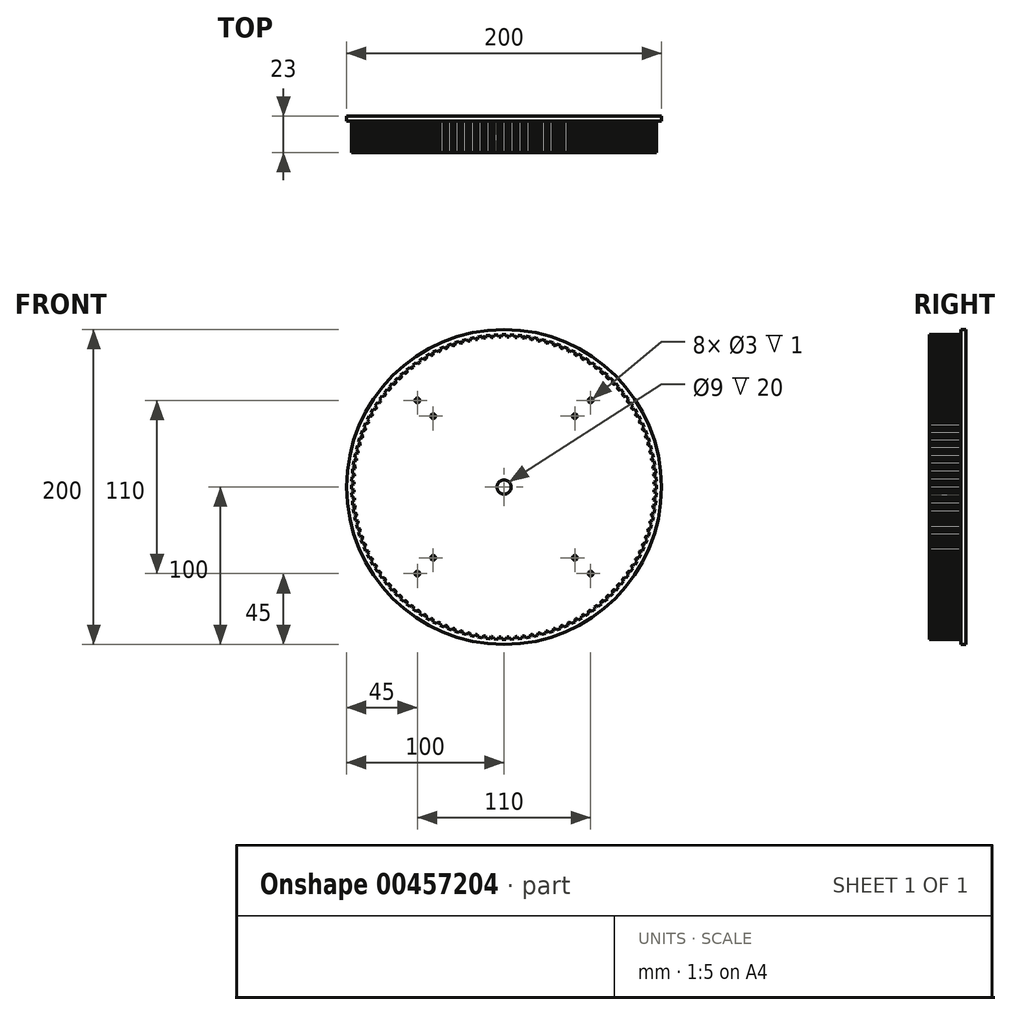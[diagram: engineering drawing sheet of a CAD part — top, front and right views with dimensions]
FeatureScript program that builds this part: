
annotation { "Feature Type Name" : "Feature", "Feature Type Description" : "" }
export const myFeature = defineFeature(function(context is Context, id is Id, definition is map)
    precondition{}
    {
        {
            var Q0;
            Q0=qCreatedBy(makeId("Front.planeOp"),FACE);
            var sketch = newSketch(context, id + "F0", { "sketchPlane" : qUnion([Q0])});
            skCircle(sketch, "E0", {"center": v(0, 0) * mm, "radius": 96.77 * mm, "construction": true});
            skLineSegment(sketch, "E1", {"start": v(0, 96.77) * mm, "end": v(0, 95.37) * mm, "construction": true});
            skCircle(sketch, "E2", {"center": v(0, 0) * mm, "radius": 95.37 * mm});
            skLineSegment(sketch, "E3", {"start": v(0, 0) * mm, "end": v(-1.27, 96.76) * mm, "construction": true});
            skLineSegment(sketch, "E4", {"start": v(0, 0) * mm, "end": v(-2.53, 96.73) * mm, "construction": true});
            skLineSegment(sketch, "E5.MirrorCS", {"start": v(0, 0) * mm, "end": v(1.27, 96.76) * mm, "construction": true});
            skLineSegment(sketch, "E6.MirrorCS", {"start": v(0, 0) * mm, "end": v(2.53, 96.73) * mm, "construction": true});
            skLineSegment(sketch, "E7", {"start": v(-1.27, 96.76) * mm, "end": v(1.27, 96.76) * mm});
            skLineSegment(sketch, "E8", {"start": v(-1.27, 96.76) * mm, "end": v(-1.88, 95.35) * mm});
            skLineSegment(sketch, "E9.MirrorCS", {"start": v(1.27, 96.76) * mm, "end": v(1.88, 95.35) * mm});
            skLineSegment(sketch, "E10.1.0", {"start": v(-6.33, 96.56) * mm, "end": v(-6.87, 95.12) * mm});
            skLineSegment(sketch, "E10.1.1", {"start": v(-6.33, 96.56) * mm, "end": v(-3.8, 96.7) * mm});
            skLineSegment(sketch, "E10.1.2", {"start": v(-3.8, 96.7) * mm, "end": v(-3.11, 95.31) * mm});
            skLineSegment(sketch, "E10.2.0", {"start": v(-11.37, 96.1) * mm, "end": v(-11.84, 94.63) * mm});
            skLineSegment(sketch, "E10.2.1", {"start": v(-11.37, 96.1) * mm, "end": v(-8.85, 96.36) * mm});
            skLineSegment(sketch, "E10.2.2", {"start": v(-8.85, 96.36) * mm, "end": v(-8.1, 95.02) * mm});
            skLineSegment(sketch, "E10.3.0", {"start": v(-16.39, 95.37) * mm, "end": v(-16.77, 93.88) * mm});
            skLineSegment(sketch, "E10.3.1", {"start": v(-16.39, 95.37) * mm, "end": v(-13.89, 95.76) * mm});
            skLineSegment(sketch, "E10.3.2", {"start": v(-13.89, 95.76) * mm, "end": v(-13.06, 94.47) * mm});
            skLineSegment(sketch, "E10.4.0", {"start": v(-21.36, 94.38) * mm, "end": v(-21.66, 92.87) * mm});
            skLineSegment(sketch, "E10.4.1", {"start": v(-21.36, 94.38) * mm, "end": v(-18.88, 94.9) * mm});
            skLineSegment(sketch, "E10.4.2", {"start": v(-18.88, 94.9) * mm, "end": v(-17.98, 93.65) * mm});
            skLineSegment(sketch, "E10.5.0", {"start": v(-26.27, 93.13) * mm, "end": v(-26.5, 91.61) * mm});
            skLineSegment(sketch, "E10.5.1", {"start": v(-26.27, 93.13) * mm, "end": v(-23.82, 93.79) * mm});
            skLineSegment(sketch, "E10.5.2", {"start": v(-23.82, 93.79) * mm, "end": v(-22.86, 92.58) * mm});
            skLineSegment(sketch, "E10.6.0", {"start": v(-31.1, 91.63) * mm, "end": v(-31.25, 90.1) * mm});
            skLineSegment(sketch, "E10.6.1", {"start": v(-31.1, 91.63) * mm, "end": v(-28.7, 92.41) * mm});
            skLineSegment(sketch, "E10.6.2", {"start": v(-28.7, 92.41) * mm, "end": v(-27.68, 91.26) * mm});
            skLineSegment(sketch, "E10.7.0", {"start": v(-35.86, 89.88) * mm, "end": v(-35.92, 88.34) * mm});
            skLineSegment(sketch, "E10.7.1", {"start": v(-35.86, 89.88) * mm, "end": v(-33.5, 90.78) * mm});
            skLineSegment(sketch, "E10.7.2", {"start": v(-33.5, 90.78) * mm, "end": v(-32.41, 89.69) * mm});
            skLineSegment(sketch, "E10.8.0", {"start": v(-40.51, 87.88) * mm, "end": v(-40.5, 86.34) * mm});
            skLineSegment(sketch, "E10.8.1", {"start": v(-40.51, 87.88) * mm, "end": v(-38.2, 88.9) * mm});
            skLineSegment(sketch, "E10.8.2", {"start": v(-38.2, 88.9) * mm, "end": v(-37.06, 87.87) * mm});
            skLineSegment(sketch, "E10.9.0", {"start": v(-45.06, 85.64) * mm, "end": v(-44.96, 84.1) * mm});
            skLineSegment(sketch, "E10.9.1", {"start": v(-45.06, 85.64) * mm, "end": v(-42.8, 86.79) * mm});
            skLineSegment(sketch, "E10.9.2", {"start": v(-42.8, 86.79) * mm, "end": v(-41.61, 85.8) * mm});
            skLineSegment(sketch, "E11", {"start": v(0, 0) * mm, "end": v(0, 96.77) * mm, "construction": true});
            skLineSegment(sketch, "E12.2.10.0", {"start": v(-49.48, 83.16) * mm, "end": v(-49.3, 81.63) * mm});
            skLineSegment(sketch, "E12.3.10.0", {"start": v(-49.48, 83.16) * mm, "end": v(-47.28, 84.43) * mm});
            skLineSegment(sketch, "E12.6.10.0", {"start": v(-47.28, 84.43) * mm, "end": v(-46.05, 83.51) * mm});
            skLineSegment(sketch, "E12.2.11.0", {"start": v(-53.76, 80.46) * mm, "end": v(-53.5, 78.94) * mm});
            skLineSegment(sketch, "E12.3.11.0", {"start": v(-53.76, 80.46) * mm, "end": v(-51.64, 81.84) * mm});
            skLineSegment(sketch, "E12.6.11.0", {"start": v(-51.64, 81.84) * mm, "end": v(-50.35, 80.99) * mm});
            skLineSegment(sketch, "E12.2.12.0", {"start": v(-57.9, 77.53) * mm, "end": v(-57.56, 76.03) * mm});
            skLineSegment(sketch, "E12.3.12.0", {"start": v(-57.9, 77.53) * mm, "end": v(-55.85, 79.02) * mm});
            skLineSegment(sketch, "E12.6.12.0", {"start": v(-55.85, 79.02) * mm, "end": v(-54.52, 78.24) * mm});
            skLineSegment(sketch, "E12.2.13.0", {"start": v(-61.88, 74.4) * mm, "end": v(-61.46, 72.92) * mm});
            skLineSegment(sketch, "E12.3.13.0", {"start": v(-61.88, 74.4) * mm, "end": v(-59.9, 76) * mm});
            skLineSegment(sketch, "E12.6.13.0", {"start": v(-59.9, 76) * mm, "end": v(-58.54, 75.28) * mm});
            skLineSegment(sketch, "E12.2.14.0", {"start": v(-65.68, 71.06) * mm, "end": v(-65.2, 69.6) * mm});
            skLineSegment(sketch, "E12.3.14.0", {"start": v(-65.68, 71.06) * mm, "end": v(-63.8, 72.75) * mm});
            skLineSegment(sketch, "E12.6.14.0", {"start": v(-63.8, 72.75) * mm, "end": v(-62.4, 72.11) * mm});
            skLineSegment(sketch, "E12.2.15.0", {"start": v(-69.31, 67.52) * mm, "end": v(-68.75, 66.1) * mm});
            skLineSegment(sketch, "E12.3.15.0", {"start": v(-69.31, 67.52) * mm, "end": v(-67.52, 69.31) * mm});
            skLineSegment(sketch, "E12.6.15.0", {"start": v(-67.52, 69.31) * mm, "end": v(-66.1, 68.75) * mm});
            skLineSegment(sketch, "E12.2.16.0", {"start": v(-72.75, 63.8) * mm, "end": v(-72.11, 62.4) * mm});
            skLineSegment(sketch, "E12.3.16.0", {"start": v(-72.75, 63.8) * mm, "end": v(-71.06, 65.68) * mm});
            skLineSegment(sketch, "E12.6.16.0", {"start": v(-71.06, 65.68) * mm, "end": v(-69.6, 65.2) * mm});
            skLineSegment(sketch, "E12.2.17.0", {"start": v(-76, 59.9) * mm, "end": v(-75.28, 58.54) * mm});
            skLineSegment(sketch, "E12.3.17.0", {"start": v(-76, 59.9) * mm, "end": v(-74.4, 61.88) * mm});
            skLineSegment(sketch, "E12.6.17.0", {"start": v(-74.4, 61.88) * mm, "end": v(-72.92, 61.46) * mm});
            skLineSegment(sketch, "E12.2.18.0", {"start": v(-79.02, 55.85) * mm, "end": v(-78.24, 54.52) * mm});
            skLineSegment(sketch, "E12.3.18.0", {"start": v(-79.02, 55.85) * mm, "end": v(-77.53, 57.9) * mm});
            skLineSegment(sketch, "E12.6.18.0", {"start": v(-77.53, 57.9) * mm, "end": v(-76.03, 57.56) * mm});
            skLineSegment(sketch, "E12.2.19.0", {"start": v(-81.84, 51.64) * mm, "end": v(-80.99, 50.35) * mm});
            skLineSegment(sketch, "E12.3.19.0", {"start": v(-81.84, 51.64) * mm, "end": v(-80.46, 53.76) * mm});
            skLineSegment(sketch, "E12.6.19.0", {"start": v(-80.46, 53.76) * mm, "end": v(-78.94, 53.5) * mm});
            skLineSegment(sketch, "E12.2.20.0", {"start": v(-84.43, 47.28) * mm, "end": v(-83.51, 46.05) * mm});
            skLineSegment(sketch, "E12.3.20.0", {"start": v(-84.43, 47.28) * mm, "end": v(-83.16, 49.48) * mm});
            skLineSegment(sketch, "E12.6.20.0", {"start": v(-83.16, 49.48) * mm, "end": v(-81.63, 49.3) * mm});
            skLineSegment(sketch, "E12.2.21.0", {"start": v(-86.79, 42.8) * mm, "end": v(-85.8, 41.61) * mm});
            skLineSegment(sketch, "E12.3.21.0", {"start": v(-86.79, 42.8) * mm, "end": v(-85.64, 45.06) * mm});
            skLineSegment(sketch, "E12.6.21.0", {"start": v(-85.64, 45.06) * mm, "end": v(-84.1, 44.96) * mm});
            skLineSegment(sketch, "E12.2.22.0", {"start": v(-88.9, 38.2) * mm, "end": v(-87.87, 37.06) * mm});
            skLineSegment(sketch, "E12.3.22.0", {"start": v(-88.9, 38.2) * mm, "end": v(-87.88, 40.51) * mm});
            skLineSegment(sketch, "E12.6.22.0", {"start": v(-87.88, 40.51) * mm, "end": v(-86.34, 40.5) * mm});
            skLineSegment(sketch, "E12.2.23.0", {"start": v(-90.78, 33.5) * mm, "end": v(-89.69, 32.41) * mm});
            skLineSegment(sketch, "E12.3.23.0", {"start": v(-90.78, 33.5) * mm, "end": v(-89.88, 35.86) * mm});
            skLineSegment(sketch, "E12.6.23.0", {"start": v(-89.88, 35.86) * mm, "end": v(-88.34, 35.92) * mm});
            skLineSegment(sketch, "E12.2.24.0", {"start": v(-92.41, 28.7) * mm, "end": v(-91.26, 27.68) * mm});
            skLineSegment(sketch, "E12.3.24.0", {"start": v(-92.41, 28.7) * mm, "end": v(-91.63, 31.1) * mm});
            skLineSegment(sketch, "E12.6.24.0", {"start": v(-91.63, 31.1) * mm, "end": v(-90.1, 31.25) * mm});
            skLineSegment(sketch, "E12.2.25.0", {"start": v(-93.79, 23.82) * mm, "end": v(-92.58, 22.86) * mm});
            skLineSegment(sketch, "E12.3.25.0", {"start": v(-93.79, 23.82) * mm, "end": v(-93.13, 26.27) * mm});
            skLineSegment(sketch, "E12.6.25.0", {"start": v(-93.13, 26.27) * mm, "end": v(-91.61, 26.5) * mm});
            skLineSegment(sketch, "E12.2.26.0", {"start": v(-94.9, 18.88) * mm, "end": v(-93.65, 17.98) * mm});
            skLineSegment(sketch, "E12.3.26.0", {"start": v(-94.9, 18.88) * mm, "end": v(-94.38, 21.36) * mm});
            skLineSegment(sketch, "E12.6.26.0", {"start": v(-94.38, 21.36) * mm, "end": v(-92.87, 21.66) * mm});
            skLineSegment(sketch, "E12.2.27.0", {"start": v(-95.76, 13.89) * mm, "end": v(-94.47, 13.06) * mm});
            skLineSegment(sketch, "E12.3.27.0", {"start": v(-95.76, 13.89) * mm, "end": v(-95.37, 16.39) * mm});
            skLineSegment(sketch, "E12.6.27.0", {"start": v(-95.37, 16.39) * mm, "end": v(-93.88, 16.77) * mm});
            skLineSegment(sketch, "E12.2.28.0", {"start": v(-96.36, 8.85) * mm, "end": v(-95.02, 8.1) * mm});
            skLineSegment(sketch, "E12.3.28.0", {"start": v(-96.36, 8.85) * mm, "end": v(-96.1, 11.37) * mm});
            skLineSegment(sketch, "E12.6.28.0", {"start": v(-96.1, 11.37) * mm, "end": v(-94.63, 11.84) * mm});
            skLineSegment(sketch, "E12.2.29.0", {"start": v(-96.7, 3.8) * mm, "end": v(-95.31, 3.11) * mm});
            skLineSegment(sketch, "E12.3.29.0", {"start": v(-96.7, 3.8) * mm, "end": v(-96.56, 6.33) * mm});
            skLineSegment(sketch, "E12.6.29.0", {"start": v(-96.56, 6.33) * mm, "end": v(-95.12, 6.87) * mm});
            skLineSegment(sketch, "E12.2.30.0", {"start": v(-96.76, -1.27) * mm, "end": v(-95.35, -1.88) * mm});
            skLineSegment(sketch, "E12.3.30.0", {"start": v(-96.76, -1.27) * mm, "end": v(-96.76, 1.27) * mm});
            skLineSegment(sketch, "E12.6.30.0", {"start": v(-96.76, 1.27) * mm, "end": v(-95.35, 1.88) * mm});
            skLineSegment(sketch, "E12.2.31.0", {"start": v(-96.56, -6.33) * mm, "end": v(-95.12, -6.87) * mm});
            skLineSegment(sketch, "E12.3.31.0", {"start": v(-96.56, -6.33) * mm, "end": v(-96.7, -3.8) * mm});
            skLineSegment(sketch, "E12.6.31.0", {"start": v(-96.7, -3.8) * mm, "end": v(-95.31, -3.11) * mm});
            skLineSegment(sketch, "E12.2.32.0", {"start": v(-96.1, -11.37) * mm, "end": v(-94.63, -11.84) * mm});
            skLineSegment(sketch, "E12.3.32.0", {"start": v(-96.1, -11.37) * mm, "end": v(-96.36, -8.85) * mm});
            skLineSegment(sketch, "E12.6.32.0", {"start": v(-96.36, -8.85) * mm, "end": v(-95.02, -8.1) * mm});
            skLineSegment(sketch, "E12.2.33.0", {"start": v(-95.37, -16.39) * mm, "end": v(-93.88, -16.77) * mm});
            skLineSegment(sketch, "E12.3.33.0", {"start": v(-95.37, -16.39) * mm, "end": v(-95.76, -13.89) * mm});
            skLineSegment(sketch, "E12.6.33.0", {"start": v(-95.76, -13.89) * mm, "end": v(-94.47, -13.06) * mm});
            skLineSegment(sketch, "E12.2.34.0", {"start": v(-94.38, -21.36) * mm, "end": v(-92.87, -21.66) * mm});
            skLineSegment(sketch, "E12.3.34.0", {"start": v(-94.38, -21.36) * mm, "end": v(-94.9, -18.88) * mm});
            skLineSegment(sketch, "E12.6.34.0", {"start": v(-94.9, -18.88) * mm, "end": v(-93.65, -17.98) * mm});
            skLineSegment(sketch, "E12.2.35.0", {"start": v(-93.13, -26.27) * mm, "end": v(-91.61, -26.5) * mm});
            skLineSegment(sketch, "E12.3.35.0", {"start": v(-93.13, -26.27) * mm, "end": v(-93.79, -23.82) * mm});
            skLineSegment(sketch, "E12.6.35.0", {"start": v(-93.79, -23.82) * mm, "end": v(-92.58, -22.86) * mm});
            skLineSegment(sketch, "E12.2.36.0", {"start": v(-91.63, -31.1) * mm, "end": v(-90.1, -31.25) * mm});
            skLineSegment(sketch, "E12.3.36.0", {"start": v(-91.63, -31.1) * mm, "end": v(-92.41, -28.7) * mm});
            skLineSegment(sketch, "E12.6.36.0", {"start": v(-92.41, -28.7) * mm, "end": v(-91.26, -27.68) * mm});
            skLineSegment(sketch, "E12.2.37.0", {"start": v(-89.88, -35.86) * mm, "end": v(-88.34, -35.92) * mm});
            skLineSegment(sketch, "E12.3.37.0", {"start": v(-89.88, -35.86) * mm, "end": v(-90.78, -33.5) * mm});
            skLineSegment(sketch, "E12.6.37.0", {"start": v(-90.78, -33.5) * mm, "end": v(-89.69, -32.41) * mm});
            skLineSegment(sketch, "E12.2.38.0", {"start": v(-87.88, -40.51) * mm, "end": v(-86.34, -40.5) * mm});
            skLineSegment(sketch, "E12.3.38.0", {"start": v(-87.88, -40.51) * mm, "end": v(-88.9, -38.2) * mm});
            skLineSegment(sketch, "E12.6.38.0", {"start": v(-88.9, -38.2) * mm, "end": v(-87.87, -37.06) * mm});
            skLineSegment(sketch, "E12.2.39.0", {"start": v(-85.64, -45.06) * mm, "end": v(-84.1, -44.96) * mm});
            skLineSegment(sketch, "E12.3.39.0", {"start": v(-85.64, -45.06) * mm, "end": v(-86.79, -42.8) * mm});
            skLineSegment(sketch, "E12.6.39.0", {"start": v(-86.79, -42.8) * mm, "end": v(-85.8, -41.61) * mm});
            skLineSegment(sketch, "E12.2.40.0", {"start": v(-83.16, -49.48) * mm, "end": v(-81.63, -49.3) * mm});
            skLineSegment(sketch, "E12.3.40.0", {"start": v(-83.16, -49.48) * mm, "end": v(-84.43, -47.28) * mm});
            skLineSegment(sketch, "E12.6.40.0", {"start": v(-84.43, -47.28) * mm, "end": v(-83.51, -46.05) * mm});
            skLineSegment(sketch, "E12.2.41.0", {"start": v(-80.46, -53.76) * mm, "end": v(-78.94, -53.5) * mm});
            skLineSegment(sketch, "E12.3.41.0", {"start": v(-80.46, -53.76) * mm, "end": v(-81.84, -51.64) * mm});
            skLineSegment(sketch, "E12.6.41.0", {"start": v(-81.84, -51.64) * mm, "end": v(-80.99, -50.35) * mm});
            skLineSegment(sketch, "E12.2.42.0", {"start": v(-77.53, -57.9) * mm, "end": v(-76.03, -57.56) * mm});
            skLineSegment(sketch, "E12.3.42.0", {"start": v(-77.53, -57.9) * mm, "end": v(-79.02, -55.85) * mm});
            skLineSegment(sketch, "E12.6.42.0", {"start": v(-79.02, -55.85) * mm, "end": v(-78.24, -54.52) * mm});
            skLineSegment(sketch, "E12.2.43.0", {"start": v(-74.4, -61.88) * mm, "end": v(-72.92, -61.46) * mm});
            skLineSegment(sketch, "E12.3.43.0", {"start": v(-74.4, -61.88) * mm, "end": v(-76, -59.9) * mm});
            skLineSegment(sketch, "E12.6.43.0", {"start": v(-76, -59.9) * mm, "end": v(-75.28, -58.54) * mm});
            skLineSegment(sketch, "E12.2.44.0", {"start": v(-71.06, -65.68) * mm, "end": v(-69.6, -65.2) * mm});
            skLineSegment(sketch, "E12.3.44.0", {"start": v(-71.06, -65.68) * mm, "end": v(-72.75, -63.8) * mm});
            skLineSegment(sketch, "E12.6.44.0", {"start": v(-72.75, -63.8) * mm, "end": v(-72.11, -62.4) * mm});
            skLineSegment(sketch, "E12.2.45.0", {"start": v(-67.52, -69.31) * mm, "end": v(-66.1, -68.75) * mm});
            skLineSegment(sketch, "E12.3.45.0", {"start": v(-67.52, -69.31) * mm, "end": v(-69.31, -67.52) * mm});
            skLineSegment(sketch, "E12.6.45.0", {"start": v(-69.31, -67.52) * mm, "end": v(-68.75, -66.1) * mm});
            skLineSegment(sketch, "E12.2.46.0", {"start": v(-63.8, -72.75) * mm, "end": v(-62.4, -72.11) * mm});
            skLineSegment(sketch, "E12.3.46.0", {"start": v(-63.8, -72.75) * mm, "end": v(-65.68, -71.06) * mm});
            skLineSegment(sketch, "E12.6.46.0", {"start": v(-65.68, -71.06) * mm, "end": v(-65.2, -69.6) * mm});
            skLineSegment(sketch, "E12.2.47.0", {"start": v(-59.9, -76) * mm, "end": v(-58.54, -75.28) * mm});
            skLineSegment(sketch, "E12.3.47.0", {"start": v(-59.9, -76) * mm, "end": v(-61.88, -74.4) * mm});
            skLineSegment(sketch, "E12.6.47.0", {"start": v(-61.88, -74.4) * mm, "end": v(-61.46, -72.92) * mm});
            skLineSegment(sketch, "E12.2.48.0", {"start": v(-55.85, -79.02) * mm, "end": v(-54.52, -78.24) * mm});
            skLineSegment(sketch, "E12.3.48.0", {"start": v(-55.85, -79.02) * mm, "end": v(-57.9, -77.53) * mm});
            skLineSegment(sketch, "E12.6.48.0", {"start": v(-57.9, -77.53) * mm, "end": v(-57.56, -76.03) * mm});
            skLineSegment(sketch, "E12.2.49.0", {"start": v(-51.64, -81.84) * mm, "end": v(-50.35, -80.99) * mm});
            skLineSegment(sketch, "E12.3.49.0", {"start": v(-51.64, -81.84) * mm, "end": v(-53.76, -80.46) * mm});
            skLineSegment(sketch, "E12.6.49.0", {"start": v(-53.76, -80.46) * mm, "end": v(-53.5, -78.94) * mm});
            skLineSegment(sketch, "E12.2.50.0", {"start": v(-47.28, -84.43) * mm, "end": v(-46.05, -83.51) * mm});
            skLineSegment(sketch, "E12.3.50.0", {"start": v(-47.28, -84.43) * mm, "end": v(-49.48, -83.16) * mm});
            skLineSegment(sketch, "E12.6.50.0", {"start": v(-49.48, -83.16) * mm, "end": v(-49.3, -81.63) * mm});
            skLineSegment(sketch, "E12.2.51.0", {"start": v(-42.8, -86.79) * mm, "end": v(-41.61, -85.8) * mm});
            skLineSegment(sketch, "E12.3.51.0", {"start": v(-42.8, -86.79) * mm, "end": v(-45.06, -85.64) * mm});
            skLineSegment(sketch, "E12.6.51.0", {"start": v(-45.06, -85.64) * mm, "end": v(-44.96, -84.1) * mm});
            skLineSegment(sketch, "E12.2.52.0", {"start": v(-38.2, -88.9) * mm, "end": v(-37.06, -87.87) * mm});
            skLineSegment(sketch, "E12.3.52.0", {"start": v(-38.2, -88.9) * mm, "end": v(-40.51, -87.88) * mm});
            skLineSegment(sketch, "E12.6.52.0", {"start": v(-40.51, -87.88) * mm, "end": v(-40.5, -86.34) * mm});
            skLineSegment(sketch, "E12.2.53.0", {"start": v(-33.5, -90.78) * mm, "end": v(-32.41, -89.69) * mm});
            skLineSegment(sketch, "E12.3.53.0", {"start": v(-33.5, -90.78) * mm, "end": v(-35.86, -89.88) * mm});
            skLineSegment(sketch, "E12.6.53.0", {"start": v(-35.86, -89.88) * mm, "end": v(-35.92, -88.34) * mm});
            skLineSegment(sketch, "E12.2.54.0", {"start": v(-28.7, -92.41) * mm, "end": v(-27.68, -91.26) * mm});
            skLineSegment(sketch, "E12.3.54.0", {"start": v(-28.7, -92.41) * mm, "end": v(-31.1, -91.63) * mm});
            skLineSegment(sketch, "E12.6.54.0", {"start": v(-31.1, -91.63) * mm, "end": v(-31.25, -90.1) * mm});
            skLineSegment(sketch, "E12.2.55.0", {"start": v(-23.82, -93.79) * mm, "end": v(-22.86, -92.58) * mm});
            skLineSegment(sketch, "E12.3.55.0", {"start": v(-23.82, -93.79) * mm, "end": v(-26.27, -93.13) * mm});
            skLineSegment(sketch, "E12.6.55.0", {"start": v(-26.27, -93.13) * mm, "end": v(-26.5, -91.61) * mm});
            skLineSegment(sketch, "E12.2.56.0", {"start": v(-18.88, -94.9) * mm, "end": v(-17.98, -93.65) * mm});
            skLineSegment(sketch, "E12.3.56.0", {"start": v(-18.88, -94.9) * mm, "end": v(-21.36, -94.38) * mm});
            skLineSegment(sketch, "E12.6.56.0", {"start": v(-21.36, -94.38) * mm, "end": v(-21.66, -92.87) * mm});
            skLineSegment(sketch, "E12.2.57.0", {"start": v(-13.89, -95.76) * mm, "end": v(-13.06, -94.47) * mm});
            skLineSegment(sketch, "E12.3.57.0", {"start": v(-13.89, -95.76) * mm, "end": v(-16.39, -95.37) * mm});
            skLineSegment(sketch, "E12.6.57.0", {"start": v(-16.39, -95.37) * mm, "end": v(-16.77, -93.88) * mm});
            skLineSegment(sketch, "E12.2.58.0", {"start": v(-8.85, -96.36) * mm, "end": v(-8.1, -95.02) * mm});
            skLineSegment(sketch, "E12.3.58.0", {"start": v(-8.85, -96.36) * mm, "end": v(-11.37, -96.1) * mm});
            skLineSegment(sketch, "E12.6.58.0", {"start": v(-11.37, -96.1) * mm, "end": v(-11.84, -94.63) * mm});
            skLineSegment(sketch, "E12.2.59.0", {"start": v(-3.8, -96.7) * mm, "end": v(-3.11, -95.31) * mm});
            skLineSegment(sketch, "E12.3.59.0", {"start": v(-3.8, -96.7) * mm, "end": v(-6.33, -96.56) * mm});
            skLineSegment(sketch, "E12.6.59.0", {"start": v(-6.33, -96.56) * mm, "end": v(-6.87, -95.12) * mm});
            skLineSegment(sketch, "E13.2.60.0", {"start": v(1.27, -96.76) * mm, "end": v(1.88, -95.35) * mm});
            skLineSegment(sketch, "E13.3.60.0", {"start": v(1.27, -96.76) * mm, "end": v(-1.27, -96.76) * mm});
            skLineSegment(sketch, "E13.6.60.0", {"start": v(-1.27, -96.76) * mm, "end": v(-1.88, -95.35) * mm});
            skLineSegment(sketch, "E13.2.61.0", {"start": v(6.33, -96.56) * mm, "end": v(6.87, -95.12) * mm});
            skLineSegment(sketch, "E13.3.61.0", {"start": v(6.33, -96.56) * mm, "end": v(3.8, -96.7) * mm});
            skLineSegment(sketch, "E13.6.61.0", {"start": v(3.8, -96.7) * mm, "end": v(3.11, -95.31) * mm});
            skLineSegment(sketch, "E13.2.62.0", {"start": v(11.37, -96.1) * mm, "end": v(11.84, -94.63) * mm});
            skLineSegment(sketch, "E13.3.62.0", {"start": v(11.37, -96.1) * mm, "end": v(8.85, -96.36) * mm});
            skLineSegment(sketch, "E13.6.62.0", {"start": v(8.85, -96.36) * mm, "end": v(8.1, -95.02) * mm});
            skLineSegment(sketch, "E13.2.63.0", {"start": v(16.39, -95.37) * mm, "end": v(16.77, -93.88) * mm});
            skLineSegment(sketch, "E13.3.63.0", {"start": v(16.39, -95.37) * mm, "end": v(13.89, -95.76) * mm});
            skLineSegment(sketch, "E13.6.63.0", {"start": v(13.89, -95.76) * mm, "end": v(13.06, -94.47) * mm});
            skLineSegment(sketch, "E13.2.64.0", {"start": v(21.36, -94.38) * mm, "end": v(21.66, -92.87) * mm});
            skLineSegment(sketch, "E13.3.64.0", {"start": v(21.36, -94.38) * mm, "end": v(18.88, -94.9) * mm});
            skLineSegment(sketch, "E13.6.64.0", {"start": v(18.88, -94.9) * mm, "end": v(17.98, -93.65) * mm});
            skLineSegment(sketch, "E13.2.65.0", {"start": v(26.27, -93.13) * mm, "end": v(26.5, -91.61) * mm});
            skLineSegment(sketch, "E13.3.65.0", {"start": v(26.27, -93.13) * mm, "end": v(23.82, -93.79) * mm});
            skLineSegment(sketch, "E13.6.65.0", {"start": v(23.82, -93.79) * mm, "end": v(22.86, -92.58) * mm});
            skLineSegment(sketch, "E13.2.66.0", {"start": v(31.1, -91.63) * mm, "end": v(31.25, -90.1) * mm});
            skLineSegment(sketch, "E13.3.66.0", {"start": v(31.1, -91.63) * mm, "end": v(28.7, -92.41) * mm});
            skLineSegment(sketch, "E13.6.66.0", {"start": v(28.7, -92.41) * mm, "end": v(27.68, -91.26) * mm});
            skLineSegment(sketch, "E13.2.67.0", {"start": v(35.86, -89.88) * mm, "end": v(35.92, -88.34) * mm});
            skLineSegment(sketch, "E13.3.67.0", {"start": v(35.86, -89.88) * mm, "end": v(33.5, -90.78) * mm});
            skLineSegment(sketch, "E13.6.67.0", {"start": v(33.5, -90.78) * mm, "end": v(32.41, -89.69) * mm});
            skLineSegment(sketch, "E13.2.68.0", {"start": v(40.51, -87.88) * mm, "end": v(40.5, -86.34) * mm});
            skLineSegment(sketch, "E13.3.68.0", {"start": v(40.51, -87.88) * mm, "end": v(38.2, -88.9) * mm});
            skLineSegment(sketch, "E13.6.68.0", {"start": v(38.2, -88.9) * mm, "end": v(37.06, -87.87) * mm});
            skLineSegment(sketch, "E13.2.69.0", {"start": v(45.06, -85.64) * mm, "end": v(44.96, -84.1) * mm});
            skLineSegment(sketch, "E13.3.69.0", {"start": v(45.06, -85.64) * mm, "end": v(42.8, -86.79) * mm});
            skLineSegment(sketch, "E13.6.69.0", {"start": v(42.8, -86.79) * mm, "end": v(41.61, -85.8) * mm});
            skLineSegment(sketch, "E13.2.70.0", {"start": v(49.48, -83.16) * mm, "end": v(49.3, -81.63) * mm});
            skLineSegment(sketch, "E13.3.70.0", {"start": v(49.48, -83.16) * mm, "end": v(47.28, -84.43) * mm});
            skLineSegment(sketch, "E13.6.70.0", {"start": v(47.28, -84.43) * mm, "end": v(46.05, -83.51) * mm});
            skLineSegment(sketch, "E13.2.71.0", {"start": v(53.76, -80.46) * mm, "end": v(53.5, -78.94) * mm});
            skLineSegment(sketch, "E13.3.71.0", {"start": v(53.76, -80.46) * mm, "end": v(51.64, -81.84) * mm});
            skLineSegment(sketch, "E13.6.71.0", {"start": v(51.64, -81.84) * mm, "end": v(50.35, -80.99) * mm});
            skLineSegment(sketch, "E13.2.72.0", {"start": v(57.9, -77.53) * mm, "end": v(57.56, -76.03) * mm});
            skLineSegment(sketch, "E13.3.72.0", {"start": v(57.9, -77.53) * mm, "end": v(55.85, -79.02) * mm});
            skLineSegment(sketch, "E13.6.72.0", {"start": v(55.85, -79.02) * mm, "end": v(54.52, -78.24) * mm});
            skLineSegment(sketch, "E13.2.73.0", {"start": v(61.88, -74.4) * mm, "end": v(61.46, -72.92) * mm});
            skLineSegment(sketch, "E13.3.73.0", {"start": v(61.88, -74.4) * mm, "end": v(59.9, -76) * mm});
            skLineSegment(sketch, "E13.6.73.0", {"start": v(59.9, -76) * mm, "end": v(58.54, -75.28) * mm});
            skLineSegment(sketch, "E13.2.74.0", {"start": v(65.68, -71.06) * mm, "end": v(65.2, -69.6) * mm});
            skLineSegment(sketch, "E13.3.74.0", {"start": v(65.68, -71.06) * mm, "end": v(63.8, -72.75) * mm});
            skLineSegment(sketch, "E13.6.74.0", {"start": v(63.8, -72.75) * mm, "end": v(62.4, -72.11) * mm});
            skLineSegment(sketch, "E13.2.75.0", {"start": v(69.31, -67.52) * mm, "end": v(68.75, -66.1) * mm});
            skLineSegment(sketch, "E13.3.75.0", {"start": v(69.31, -67.52) * mm, "end": v(67.52, -69.31) * mm});
            skLineSegment(sketch, "E13.6.75.0", {"start": v(67.52, -69.31) * mm, "end": v(66.1, -68.75) * mm});
            skLineSegment(sketch, "E13.2.76.0", {"start": v(72.75, -63.8) * mm, "end": v(72.11, -62.4) * mm});
            skLineSegment(sketch, "E13.3.76.0", {"start": v(72.75, -63.8) * mm, "end": v(71.06, -65.68) * mm});
            skLineSegment(sketch, "E13.6.76.0", {"start": v(71.06, -65.68) * mm, "end": v(69.6, -65.2) * mm});
            skLineSegment(sketch, "E13.2.77.0", {"start": v(76, -59.9) * mm, "end": v(75.28, -58.54) * mm});
            skLineSegment(sketch, "E13.3.77.0", {"start": v(76, -59.9) * mm, "end": v(74.4, -61.88) * mm});
            skLineSegment(sketch, "E13.6.77.0", {"start": v(74.4, -61.88) * mm, "end": v(72.92, -61.46) * mm});
            skLineSegment(sketch, "E13.2.78.0", {"start": v(79.02, -55.85) * mm, "end": v(78.24, -54.52) * mm});
            skLineSegment(sketch, "E13.3.78.0", {"start": v(79.02, -55.85) * mm, "end": v(77.53, -57.9) * mm});
            skLineSegment(sketch, "E13.6.78.0", {"start": v(77.53, -57.9) * mm, "end": v(76.03, -57.56) * mm});
            skLineSegment(sketch, "E13.2.79.0", {"start": v(81.84, -51.64) * mm, "end": v(80.99, -50.35) * mm});
            skLineSegment(sketch, "E13.3.79.0", {"start": v(81.84, -51.64) * mm, "end": v(80.46, -53.76) * mm});
            skLineSegment(sketch, "E13.6.79.0", {"start": v(80.46, -53.76) * mm, "end": v(78.94, -53.5) * mm});
            skLineSegment(sketch, "E13.2.80.0", {"start": v(84.43, -47.28) * mm, "end": v(83.51, -46.05) * mm});
            skLineSegment(sketch, "E13.3.80.0", {"start": v(84.43, -47.28) * mm, "end": v(83.16, -49.48) * mm});
            skLineSegment(sketch, "E13.6.80.0", {"start": v(83.16, -49.48) * mm, "end": v(81.63, -49.3) * mm});
            skLineSegment(sketch, "E13.2.81.0", {"start": v(86.79, -42.8) * mm, "end": v(85.8, -41.61) * mm});
            skLineSegment(sketch, "E13.3.81.0", {"start": v(86.79, -42.8) * mm, "end": v(85.64, -45.06) * mm});
            skLineSegment(sketch, "E13.6.81.0", {"start": v(85.64, -45.06) * mm, "end": v(84.1, -44.96) * mm});
            skLineSegment(sketch, "E13.2.82.0", {"start": v(88.9, -38.2) * mm, "end": v(87.87, -37.06) * mm});
            skLineSegment(sketch, "E13.3.82.0", {"start": v(88.9, -38.2) * mm, "end": v(87.88, -40.51) * mm});
            skLineSegment(sketch, "E13.6.82.0", {"start": v(87.88, -40.51) * mm, "end": v(86.34, -40.5) * mm});
            skLineSegment(sketch, "E13.2.83.0", {"start": v(90.78, -33.5) * mm, "end": v(89.69, -32.41) * mm});
            skLineSegment(sketch, "E13.3.83.0", {"start": v(90.78, -33.5) * mm, "end": v(89.88, -35.86) * mm});
            skLineSegment(sketch, "E13.6.83.0", {"start": v(89.88, -35.86) * mm, "end": v(88.34, -35.92) * mm});
            skLineSegment(sketch, "E13.2.84.0", {"start": v(92.41, -28.7) * mm, "end": v(91.26, -27.68) * mm});
            skLineSegment(sketch, "E13.3.84.0", {"start": v(92.41, -28.7) * mm, "end": v(91.63, -31.1) * mm});
            skLineSegment(sketch, "E13.6.84.0", {"start": v(91.63, -31.1) * mm, "end": v(90.1, -31.25) * mm});
            skLineSegment(sketch, "E13.2.85.0", {"start": v(93.79, -23.82) * mm, "end": v(92.58, -22.86) * mm});
            skLineSegment(sketch, "E13.3.85.0", {"start": v(93.79, -23.82) * mm, "end": v(93.13, -26.27) * mm});
            skLineSegment(sketch, "E13.6.85.0", {"start": v(93.13, -26.27) * mm, "end": v(91.61, -26.5) * mm});
            skLineSegment(sketch, "E13.2.86.0", {"start": v(94.9, -18.88) * mm, "end": v(93.65, -17.98) * mm});
            skLineSegment(sketch, "E13.3.86.0", {"start": v(94.9, -18.88) * mm, "end": v(94.38, -21.36) * mm});
            skLineSegment(sketch, "E13.6.86.0", {"start": v(94.38, -21.36) * mm, "end": v(92.87, -21.66) * mm});
            skLineSegment(sketch, "E13.2.87.0", {"start": v(95.76, -13.89) * mm, "end": v(94.47, -13.06) * mm});
            skLineSegment(sketch, "E13.3.87.0", {"start": v(95.76, -13.89) * mm, "end": v(95.37, -16.39) * mm});
            skLineSegment(sketch, "E13.6.87.0", {"start": v(95.37, -16.39) * mm, "end": v(93.88, -16.77) * mm});
            skLineSegment(sketch, "E13.2.88.0", {"start": v(96.36, -8.85) * mm, "end": v(95.02, -8.1) * mm});
            skLineSegment(sketch, "E13.3.88.0", {"start": v(96.36, -8.85) * mm, "end": v(96.1, -11.37) * mm});
            skLineSegment(sketch, "E13.6.88.0", {"start": v(96.1, -11.37) * mm, "end": v(94.63, -11.84) * mm});
            skLineSegment(sketch, "E13.2.89.0", {"start": v(96.7, -3.8) * mm, "end": v(95.31, -3.11) * mm});
            skLineSegment(sketch, "E13.3.89.0", {"start": v(96.7, -3.8) * mm, "end": v(96.56, -6.33) * mm});
            skLineSegment(sketch, "E13.6.89.0", {"start": v(96.56, -6.33) * mm, "end": v(95.12, -6.87) * mm});
            skLineSegment(sketch, "E13.2.90.0", {"start": v(96.76, 1.27) * mm, "end": v(95.35, 1.88) * mm});
            skLineSegment(sketch, "E13.3.90.0", {"start": v(96.76, 1.27) * mm, "end": v(96.76, -1.27) * mm});
            skLineSegment(sketch, "E13.6.90.0", {"start": v(96.76, -1.27) * mm, "end": v(95.35, -1.88) * mm});
            skLineSegment(sketch, "E13.2.91.0", {"start": v(96.56, 6.33) * mm, "end": v(95.12, 6.87) * mm});
            skLineSegment(sketch, "E13.3.91.0", {"start": v(96.56, 6.33) * mm, "end": v(96.7, 3.8) * mm});
            skLineSegment(sketch, "E13.6.91.0", {"start": v(96.7, 3.8) * mm, "end": v(95.31, 3.11) * mm});
            skLineSegment(sketch, "E13.2.92.0", {"start": v(96.1, 11.37) * mm, "end": v(94.63, 11.84) * mm});
            skLineSegment(sketch, "E13.3.92.0", {"start": v(96.1, 11.37) * mm, "end": v(96.36, 8.85) * mm});
            skLineSegment(sketch, "E13.6.92.0", {"start": v(96.36, 8.85) * mm, "end": v(95.02, 8.1) * mm});
            skLineSegment(sketch, "E13.2.93.0", {"start": v(95.37, 16.39) * mm, "end": v(93.88, 16.77) * mm});
            skLineSegment(sketch, "E13.3.93.0", {"start": v(95.37, 16.39) * mm, "end": v(95.76, 13.89) * mm});
            skLineSegment(sketch, "E13.6.93.0", {"start": v(95.76, 13.89) * mm, "end": v(94.47, 13.06) * mm});
            skLineSegment(sketch, "E13.2.94.0", {"start": v(94.38, 21.36) * mm, "end": v(92.87, 21.66) * mm});
            skLineSegment(sketch, "E13.3.94.0", {"start": v(94.38, 21.36) * mm, "end": v(94.9, 18.88) * mm});
            skLineSegment(sketch, "E13.6.94.0", {"start": v(94.9, 18.88) * mm, "end": v(93.65, 17.98) * mm});
            skLineSegment(sketch, "E13.2.95.0", {"start": v(93.13, 26.27) * mm, "end": v(91.61, 26.5) * mm});
            skLineSegment(sketch, "E13.3.95.0", {"start": v(93.13, 26.27) * mm, "end": v(93.79, 23.82) * mm});
            skLineSegment(sketch, "E13.6.95.0", {"start": v(93.79, 23.82) * mm, "end": v(92.58, 22.86) * mm});
            skLineSegment(sketch, "E13.2.96.0", {"start": v(91.63, 31.1) * mm, "end": v(90.1, 31.25) * mm});
            skLineSegment(sketch, "E13.3.96.0", {"start": v(91.63, 31.1) * mm, "end": v(92.41, 28.7) * mm});
            skLineSegment(sketch, "E13.6.96.0", {"start": v(92.41, 28.7) * mm, "end": v(91.26, 27.68) * mm});
            skLineSegment(sketch, "E13.2.97.0", {"start": v(89.88, 35.86) * mm, "end": v(88.34, 35.92) * mm});
            skLineSegment(sketch, "E13.3.97.0", {"start": v(89.88, 35.86) * mm, "end": v(90.78, 33.5) * mm});
            skLineSegment(sketch, "E13.6.97.0", {"start": v(90.78, 33.5) * mm, "end": v(89.69, 32.41) * mm});
            skLineSegment(sketch, "E13.2.98.0", {"start": v(87.88, 40.51) * mm, "end": v(86.34, 40.5) * mm});
            skLineSegment(sketch, "E13.3.98.0", {"start": v(87.88, 40.51) * mm, "end": v(88.9, 38.2) * mm});
            skLineSegment(sketch, "E13.6.98.0", {"start": v(88.9, 38.2) * mm, "end": v(87.87, 37.06) * mm});
            skLineSegment(sketch, "E13.2.99.0", {"start": v(85.64, 45.06) * mm, "end": v(84.1, 44.96) * mm});
            skLineSegment(sketch, "E13.3.99.0", {"start": v(85.64, 45.06) * mm, "end": v(86.79, 42.8) * mm});
            skLineSegment(sketch, "E13.6.99.0", {"start": v(86.79, 42.8) * mm, "end": v(85.8, 41.61) * mm});
            skLineSegment(sketch, "E13.2.100.0", {"start": v(83.16, 49.48) * mm, "end": v(81.63, 49.3) * mm});
            skLineSegment(sketch, "E13.3.100.0", {"start": v(83.16, 49.48) * mm, "end": v(84.43, 47.28) * mm});
            skLineSegment(sketch, "E13.6.100.0", {"start": v(84.43, 47.28) * mm, "end": v(83.51, 46.05) * mm});
            skLineSegment(sketch, "E13.2.101.0", {"start": v(80.46, 53.76) * mm, "end": v(78.94, 53.5) * mm});
            skLineSegment(sketch, "E13.3.101.0", {"start": v(80.46, 53.76) * mm, "end": v(81.84, 51.64) * mm});
            skLineSegment(sketch, "E13.6.101.0", {"start": v(81.84, 51.64) * mm, "end": v(80.99, 50.35) * mm});
            skLineSegment(sketch, "E13.2.102.0", {"start": v(77.53, 57.9) * mm, "end": v(76.03, 57.56) * mm});
            skLineSegment(sketch, "E13.3.102.0", {"start": v(77.53, 57.9) * mm, "end": v(79.02, 55.85) * mm});
            skLineSegment(sketch, "E13.6.102.0", {"start": v(79.02, 55.85) * mm, "end": v(78.24, 54.52) * mm});
            skLineSegment(sketch, "E13.2.103.0", {"start": v(74.4, 61.88) * mm, "end": v(72.92, 61.46) * mm});
            skLineSegment(sketch, "E13.3.103.0", {"start": v(74.4, 61.88) * mm, "end": v(76, 59.9) * mm});
            skLineSegment(sketch, "E13.6.103.0", {"start": v(76, 59.9) * mm, "end": v(75.28, 58.54) * mm});
            skLineSegment(sketch, "E13.2.104.0", {"start": v(71.06, 65.68) * mm, "end": v(69.6, 65.2) * mm});
            skLineSegment(sketch, "E13.3.104.0", {"start": v(71.06, 65.68) * mm, "end": v(72.75, 63.8) * mm});
            skLineSegment(sketch, "E13.6.104.0", {"start": v(72.75, 63.8) * mm, "end": v(72.11, 62.4) * mm});
            skLineSegment(sketch, "E13.2.105.0", {"start": v(67.52, 69.31) * mm, "end": v(66.1, 68.75) * mm});
            skLineSegment(sketch, "E13.3.105.0", {"start": v(67.52, 69.31) * mm, "end": v(69.31, 67.52) * mm});
            skLineSegment(sketch, "E13.6.105.0", {"start": v(69.31, 67.52) * mm, "end": v(68.75, 66.1) * mm});
            skLineSegment(sketch, "E13.2.106.0", {"start": v(63.8, 72.75) * mm, "end": v(62.4, 72.11) * mm});
            skLineSegment(sketch, "E13.3.106.0", {"start": v(63.8, 72.75) * mm, "end": v(65.68, 71.06) * mm});
            skLineSegment(sketch, "E13.6.106.0", {"start": v(65.68, 71.06) * mm, "end": v(65.2, 69.6) * mm});
            skLineSegment(sketch, "E13.2.107.0", {"start": v(59.9, 76) * mm, "end": v(58.54, 75.28) * mm});
            skLineSegment(sketch, "E13.3.107.0", {"start": v(59.9, 76) * mm, "end": v(61.88, 74.4) * mm});
            skLineSegment(sketch, "E13.6.107.0", {"start": v(61.88, 74.4) * mm, "end": v(61.46, 72.92) * mm});
            skLineSegment(sketch, "E13.2.108.0", {"start": v(55.85, 79.02) * mm, "end": v(54.52, 78.24) * mm});
            skLineSegment(sketch, "E13.3.108.0", {"start": v(55.85, 79.02) * mm, "end": v(57.9, 77.53) * mm});
            skLineSegment(sketch, "E13.6.108.0", {"start": v(57.9, 77.53) * mm, "end": v(57.56, 76.03) * mm});
            skLineSegment(sketch, "E13.2.109.0", {"start": v(51.64, 81.84) * mm, "end": v(50.35, 80.99) * mm});
            skLineSegment(sketch, "E13.3.109.0", {"start": v(51.64, 81.84) * mm, "end": v(53.76, 80.46) * mm});
            skLineSegment(sketch, "E13.6.109.0", {"start": v(53.76, 80.46) * mm, "end": v(53.5, 78.94) * mm});
            skLineSegment(sketch, "E13.2.110.0", {"start": v(47.28, 84.43) * mm, "end": v(46.05, 83.51) * mm});
            skLineSegment(sketch, "E13.3.110.0", {"start": v(47.28, 84.43) * mm, "end": v(49.48, 83.16) * mm});
            skLineSegment(sketch, "E13.6.110.0", {"start": v(49.48, 83.16) * mm, "end": v(49.3, 81.63) * mm});
            skLineSegment(sketch, "E13.2.111.0", {"start": v(42.8, 86.79) * mm, "end": v(41.61, 85.8) * mm});
            skLineSegment(sketch, "E13.3.111.0", {"start": v(42.8, 86.79) * mm, "end": v(45.06, 85.64) * mm});
            skLineSegment(sketch, "E13.6.111.0", {"start": v(45.06, 85.64) * mm, "end": v(44.96, 84.1) * mm});
            skLineSegment(sketch, "E13.2.112.0", {"start": v(38.2, 88.9) * mm, "end": v(37.06, 87.87) * mm});
            skLineSegment(sketch, "E13.3.112.0", {"start": v(38.2, 88.9) * mm, "end": v(40.51, 87.88) * mm});
            skLineSegment(sketch, "E13.6.112.0", {"start": v(40.51, 87.88) * mm, "end": v(40.5, 86.34) * mm});
            skLineSegment(sketch, "E13.2.113.0", {"start": v(33.5, 90.78) * mm, "end": v(32.41, 89.69) * mm});
            skLineSegment(sketch, "E13.3.113.0", {"start": v(33.5, 90.78) * mm, "end": v(35.86, 89.88) * mm});
            skLineSegment(sketch, "E13.6.113.0", {"start": v(35.86, 89.88) * mm, "end": v(35.92, 88.34) * mm});
            skLineSegment(sketch, "E13.2.114.0", {"start": v(28.7, 92.41) * mm, "end": v(27.68, 91.26) * mm});
            skLineSegment(sketch, "E13.3.114.0", {"start": v(28.7, 92.41) * mm, "end": v(31.1, 91.63) * mm});
            skLineSegment(sketch, "E13.6.114.0", {"start": v(31.1, 91.63) * mm, "end": v(31.25, 90.1) * mm});
            skLineSegment(sketch, "E13.2.115.0", {"start": v(23.82, 93.79) * mm, "end": v(22.86, 92.58) * mm});
            skLineSegment(sketch, "E13.3.115.0", {"start": v(23.82, 93.79) * mm, "end": v(26.27, 93.13) * mm});
            skLineSegment(sketch, "E13.6.115.0", {"start": v(26.27, 93.13) * mm, "end": v(26.5, 91.61) * mm});
            skLineSegment(sketch, "E13.2.116.0", {"start": v(18.88, 94.9) * mm, "end": v(17.98, 93.65) * mm});
            skLineSegment(sketch, "E13.3.116.0", {"start": v(18.88, 94.9) * mm, "end": v(21.36, 94.38) * mm});
            skLineSegment(sketch, "E13.6.116.0", {"start": v(21.36, 94.38) * mm, "end": v(21.66, 92.87) * mm});
            skLineSegment(sketch, "E13.2.117.0", {"start": v(13.89, 95.76) * mm, "end": v(13.06, 94.47) * mm});
            skLineSegment(sketch, "E13.3.117.0", {"start": v(13.89, 95.76) * mm, "end": v(16.39, 95.37) * mm});
            skLineSegment(sketch, "E13.6.117.0", {"start": v(16.39, 95.37) * mm, "end": v(16.77, 93.88) * mm});
            skLineSegment(sketch, "E13.2.118.0", {"start": v(8.85, 96.36) * mm, "end": v(8.1, 95.02) * mm});
            skLineSegment(sketch, "E13.3.118.0", {"start": v(8.85, 96.36) * mm, "end": v(11.37, 96.1) * mm});
            skLineSegment(sketch, "E13.6.118.0", {"start": v(11.37, 96.1) * mm, "end": v(11.84, 94.63) * mm});
            skLineSegment(sketch, "E13.2.119.0", {"start": v(3.8, 96.7) * mm, "end": v(3.11, 95.31) * mm});
            skLineSegment(sketch, "E13.3.119.0", {"start": v(3.8, 96.7) * mm, "end": v(6.33, 96.56) * mm});
            skLineSegment(sketch, "E13.6.119.0", {"start": v(6.33, 96.56) * mm, "end": v(6.87, 95.12) * mm});
            skCircle(sketch, "E14", {"center": v(0, 0) * mm, "radius": 4.5 * mm});
            skSolve(sketch);
        }
        {
            var Q0;
            Q0=qSketchRegion(id+"F0",true);
            extrude(context, id + "F1", {"entities" : qUnion([Q0]), "depth" : 20 * mm, "offsetDistance" : 25 * mm});
        }
        {
            var Q0;
            Q0=makeQuery(id+"F1.opExtrude","CAP_FACE",FACE,{"disambiguationData":[OSD([sQuery(id+"F0.wireOp",EDGE,"E2"),sQuery(id+"F0.wireOp",EDGE,"E7"),sQuery(id+"F0.wireOp",EDGE,"E8"),sQuery(id+"F0.wireOp",EDGE,"E9.MirrorCS"),sQuery(id+"F0.wireOp",EDGE,"E10.1.0"),sQuery(id+"F0.wireOp",EDGE,"E10.1.1"),sQuery(id+"F0.wireOp",EDGE,"E10.1.2"),sQuery(id+"F0.wireOp",EDGE,"E10.2.0"),sQuery(id+"F0.wireOp",EDGE,"E10.2.1"),sQuery(id+"F0.wireOp",EDGE,"E10.2.2"),sQuery(id+"F0.wireOp",EDGE,"E10.3.0"),sQuery(id+"F0.wireOp",EDGE,"E10.3.1"),sQuery(id+"F0.wireOp",EDGE,"E10.3.2"),sQuery(id+"F0.wireOp",EDGE,"E10.4.0"),sQuery(id+"F0.wireOp",EDGE,"E10.4.1"),sQuery(id+"F0.wireOp",EDGE,"E10.4.2"),sQuery(id+"F0.wireOp",EDGE,"E10.5.0"),sQuery(id+"F0.wireOp",EDGE,"E10.5.1"),sQuery(id+"F0.wireOp",EDGE,"E10.5.2"),sQuery(id+"F0.wireOp",EDGE,"E10.6.0"),sQuery(id+"F0.wireOp",EDGE,"E10.6.1"),sQuery(id+"F0.wireOp",EDGE,"E10.6.2"),sQuery(id+"F0.wireOp",EDGE,"E10.7.0"),sQuery(id+"F0.wireOp",EDGE,"E10.7.1"),sQuery(id+"F0.wireOp",EDGE,"E10.7.2"),sQuery(id+"F0.wireOp",EDGE,"E10.8.0"),sQuery(id+"F0.wireOp",EDGE,"E10.8.1"),sQuery(id+"F0.wireOp",EDGE,"E10.8.2"),sQuery(id+"F0.wireOp",EDGE,"E10.9.0"),sQuery(id+"F0.wireOp",EDGE,"E10.9.1"),sQuery(id+"F0.wireOp",EDGE,"E10.9.2"),sQuery(id+"F0.wireOp",EDGE,"E12.2.10.0"),sQuery(id+"F0.wireOp",EDGE,"E12.3.10.0"),sQuery(id+"F0.wireOp",EDGE,"E12.6.10.0"),sQuery(id+"F0.wireOp",EDGE,"E12.2.11.0"),sQuery(id+"F0.wireOp",EDGE,"E12.3.11.0"),sQuery(id+"F0.wireOp",EDGE,"E12.6.11.0"),sQuery(id+"F0.wireOp",EDGE,"E12.2.12.0"),sQuery(id+"F0.wireOp",EDGE,"E12.3.12.0"),sQuery(id+"F0.wireOp",EDGE,"E12.6.12.0"),sQuery(id+"F0.wireOp",EDGE,"E12.2.13.0"),sQuery(id+"F0.wireOp",EDGE,"E12.3.13.0"),sQuery(id+"F0.wireOp",EDGE,"E12.6.13.0"),sQuery(id+"F0.wireOp",EDGE,"E12.2.14.0"),sQuery(id+"F0.wireOp",EDGE,"E12.3.14.0"),sQuery(id+"F0.wireOp",EDGE,"E12.6.14.0"),sQuery(id+"F0.wireOp",EDGE,"E12.2.15.0"),sQuery(id+"F0.wireOp",EDGE,"E12.3.15.0"),sQuery(id+"F0.wireOp",EDGE,"E12.6.15.0"),sQuery(id+"F0.wireOp",EDGE,"E12.2.16.0"),sQuery(id+"F0.wireOp",EDGE,"E12.3.16.0"),sQuery(id+"F0.wireOp",EDGE,"E12.6.16.0"),sQuery(id+"F0.wireOp",EDGE,"E12.2.17.0"),sQuery(id+"F0.wireOp",EDGE,"E12.3.17.0"),sQuery(id+"F0.wireOp",EDGE,"E12.6.17.0"),sQuery(id+"F0.wireOp",EDGE,"E12.2.18.0"),sQuery(id+"F0.wireOp",EDGE,"E12.3.18.0"),sQuery(id+"F0.wireOp",EDGE,"E12.6.18.0"),sQuery(id+"F0.wireOp",EDGE,"E12.2.19.0"),sQuery(id+"F0.wireOp",EDGE,"E12.3.19.0"),sQuery(id+"F0.wireOp",EDGE,"E12.6.19.0"),sQuery(id+"F0.wireOp",EDGE,"E12.2.20.0"),sQuery(id+"F0.wireOp",EDGE,"E12.3.20.0"),sQuery(id+"F0.wireOp",EDGE,"E12.6.20.0"),sQuery(id+"F0.wireOp",EDGE,"E12.2.21.0"),sQuery(id+"F0.wireOp",EDGE,"E12.3.21.0"),sQuery(id+"F0.wireOp",EDGE,"E12.6.21.0"),sQuery(id+"F0.wireOp",EDGE,"E12.2.22.0"),sQuery(id+"F0.wireOp",EDGE,"E12.3.22.0"),sQuery(id+"F0.wireOp",EDGE,"E12.6.22.0"),sQuery(id+"F0.wireOp",EDGE,"E12.2.23.0"),sQuery(id+"F0.wireOp",EDGE,"E12.3.23.0"),sQuery(id+"F0.wireOp",EDGE,"E12.6.23.0"),sQuery(id+"F0.wireOp",EDGE,"E12.2.24.0"),sQuery(id+"F0.wireOp",EDGE,"E12.3.24.0"),sQuery(id+"F0.wireOp",EDGE,"E12.6.24.0"),sQuery(id+"F0.wireOp",EDGE,"E12.2.25.0"),sQuery(id+"F0.wireOp",EDGE,"E12.3.25.0"),sQuery(id+"F0.wireOp",EDGE,"E12.6.25.0"),sQuery(id+"F0.wireOp",EDGE,"E12.2.26.0"),sQuery(id+"F0.wireOp",EDGE,"E12.3.26.0"),sQuery(id+"F0.wireOp",EDGE,"E12.6.26.0"),sQuery(id+"F0.wireOp",EDGE,"E12.2.27.0"),sQuery(id+"F0.wireOp",EDGE,"E12.3.27.0"),sQuery(id+"F0.wireOp",EDGE,"E12.6.27.0"),sQuery(id+"F0.wireOp",EDGE,"E12.2.28.0"),sQuery(id+"F0.wireOp",EDGE,"E12.3.28.0"),sQuery(id+"F0.wireOp",EDGE,"E12.6.28.0"),sQuery(id+"F0.wireOp",EDGE,"E12.2.29.0"),sQuery(id+"F0.wireOp",EDGE,"E12.3.29.0"),sQuery(id+"F0.wireOp",EDGE,"E12.6.29.0"),sQuery(id+"F0.wireOp",EDGE,"E12.2.30.0"),sQuery(id+"F0.wireOp",EDGE,"E12.3.30.0"),sQuery(id+"F0.wireOp",EDGE,"E12.6.30.0"),sQuery(id+"F0.wireOp",EDGE,"E12.2.31.0"),sQuery(id+"F0.wireOp",EDGE,"E12.3.31.0"),sQuery(id+"F0.wireOp",EDGE,"E12.6.31.0"),sQuery(id+"F0.wireOp",EDGE,"E12.2.32.0"),sQuery(id+"F0.wireOp",EDGE,"E12.3.32.0"),sQuery(id+"F0.wireOp",EDGE,"E12.6.32.0"),sQuery(id+"F0.wireOp",EDGE,"E12.2.33.0"),sQuery(id+"F0.wireOp",EDGE,"E12.3.33.0"),sQuery(id+"F0.wireOp",EDGE,"E12.6.33.0"),sQuery(id+"F0.wireOp",EDGE,"E12.2.34.0"),sQuery(id+"F0.wireOp",EDGE,"E12.3.34.0"),sQuery(id+"F0.wireOp",EDGE,"E12.6.34.0"),sQuery(id+"F0.wireOp",EDGE,"E12.2.35.0"),sQuery(id+"F0.wireOp",EDGE,"E12.3.35.0"),sQuery(id+"F0.wireOp",EDGE,"E12.6.35.0"),sQuery(id+"F0.wireOp",EDGE,"E12.2.36.0"),sQuery(id+"F0.wireOp",EDGE,"E12.3.36.0"),sQuery(id+"F0.wireOp",EDGE,"E12.6.36.0"),sQuery(id+"F0.wireOp",EDGE,"E12.2.37.0"),sQuery(id+"F0.wireOp",EDGE,"E12.3.37.0"),sQuery(id+"F0.wireOp",EDGE,"E12.6.37.0"),sQuery(id+"F0.wireOp",EDGE,"E12.2.38.0"),sQuery(id+"F0.wireOp",EDGE,"E12.3.38.0"),sQuery(id+"F0.wireOp",EDGE,"E12.6.38.0"),sQuery(id+"F0.wireOp",EDGE,"E12.2.39.0"),sQuery(id+"F0.wireOp",EDGE,"E12.3.39.0"),sQuery(id+"F0.wireOp",EDGE,"E12.6.39.0"),sQuery(id+"F0.wireOp",EDGE,"E12.2.40.0"),sQuery(id+"F0.wireOp",EDGE,"E12.3.40.0"),sQuery(id+"F0.wireOp",EDGE,"E12.6.40.0"),sQuery(id+"F0.wireOp",EDGE,"E12.2.41.0"),sQuery(id+"F0.wireOp",EDGE,"E12.3.41.0"),sQuery(id+"F0.wireOp",EDGE,"E12.6.41.0"),sQuery(id+"F0.wireOp",EDGE,"E12.2.42.0"),sQuery(id+"F0.wireOp",EDGE,"E12.3.42.0"),sQuery(id+"F0.wireOp",EDGE,"E12.6.42.0"),sQuery(id+"F0.wireOp",EDGE,"E12.2.43.0"),sQuery(id+"F0.wireOp",EDGE,"E12.3.43.0"),sQuery(id+"F0.wireOp",EDGE,"E12.6.43.0"),sQuery(id+"F0.wireOp",EDGE,"E12.2.44.0"),sQuery(id+"F0.wireOp",EDGE,"E12.3.44.0"),sQuery(id+"F0.wireOp",EDGE,"E12.6.44.0"),sQuery(id+"F0.wireOp",EDGE,"E12.2.45.0"),sQuery(id+"F0.wireOp",EDGE,"E12.3.45.0"),sQuery(id+"F0.wireOp",EDGE,"E12.6.45.0"),sQuery(id+"F0.wireOp",EDGE,"E12.2.46.0"),sQuery(id+"F0.wireOp",EDGE,"E12.3.46.0"),sQuery(id+"F0.wireOp",EDGE,"E12.6.46.0"),sQuery(id+"F0.wireOp",EDGE,"E12.2.47.0"),sQuery(id+"F0.wireOp",EDGE,"E12.3.47.0"),sQuery(id+"F0.wireOp",EDGE,"E12.6.47.0"),sQuery(id+"F0.wireOp",EDGE,"E12.2.48.0"),sQuery(id+"F0.wireOp",EDGE,"E12.3.48.0"),sQuery(id+"F0.wireOp",EDGE,"E12.6.48.0"),sQuery(id+"F0.wireOp",EDGE,"E12.2.49.0"),sQuery(id+"F0.wireOp",EDGE,"E12.3.49.0"),sQuery(id+"F0.wireOp",EDGE,"E12.6.49.0"),sQuery(id+"F0.wireOp",EDGE,"E12.2.50.0"),sQuery(id+"F0.wireOp",EDGE,"E12.3.50.0"),sQuery(id+"F0.wireOp",EDGE,"E12.6.50.0"),sQuery(id+"F0.wireOp",EDGE,"E12.2.51.0"),sQuery(id+"F0.wireOp",EDGE,"E12.3.51.0"),sQuery(id+"F0.wireOp",EDGE,"E12.6.51.0"),sQuery(id+"F0.wireOp",EDGE,"E12.2.52.0"),sQuery(id+"F0.wireOp",EDGE,"E12.3.52.0"),sQuery(id+"F0.wireOp",EDGE,"E12.6.52.0"),sQuery(id+"F0.wireOp",EDGE,"E12.2.53.0"),sQuery(id+"F0.wireOp",EDGE,"E12.3.53.0"),sQuery(id+"F0.wireOp",EDGE,"E12.6.53.0"),sQuery(id+"F0.wireOp",EDGE,"E12.2.54.0"),sQuery(id+"F0.wireOp",EDGE,"E12.3.54.0"),sQuery(id+"F0.wireOp",EDGE,"E12.6.54.0"),sQuery(id+"F0.wireOp",EDGE,"E12.2.55.0"),sQuery(id+"F0.wireOp",EDGE,"E12.3.55.0"),sQuery(id+"F0.wireOp",EDGE,"E12.6.55.0"),sQuery(id+"F0.wireOp",EDGE,"E12.2.56.0"),sQuery(id+"F0.wireOp",EDGE,"E12.3.56.0"),sQuery(id+"F0.wireOp",EDGE,"E12.6.56.0"),sQuery(id+"F0.wireOp",EDGE,"E12.2.57.0"),sQuery(id+"F0.wireOp",EDGE,"E12.3.57.0"),sQuery(id+"F0.wireOp",EDGE,"E12.6.57.0"),sQuery(id+"F0.wireOp",EDGE,"E12.2.58.0"),sQuery(id+"F0.wireOp",EDGE,"E12.3.58.0"),sQuery(id+"F0.wireOp",EDGE,"E12.6.58.0"),sQuery(id+"F0.wireOp",EDGE,"E12.2.59.0"),sQuery(id+"F0.wireOp",EDGE,"E12.3.59.0"),sQuery(id+"F0.wireOp",EDGE,"E12.6.59.0"),sQuery(id+"F0.wireOp",EDGE,"E13.2.60.0"),sQuery(id+"F0.wireOp",EDGE,"E13.3.60.0"),sQuery(id+"F0.wireOp",EDGE,"E13.6.60.0"),sQuery(id+"F0.wireOp",EDGE,"E13.2.61.0"),sQuery(id+"F0.wireOp",EDGE,"E13.3.61.0"),sQuery(id+"F0.wireOp",EDGE,"E13.6.61.0"),sQuery(id+"F0.wireOp",EDGE,"E13.2.62.0"),sQuery(id+"F0.wireOp",EDGE,"E13.3.62.0"),sQuery(id+"F0.wireOp",EDGE,"E13.6.62.0"),sQuery(id+"F0.wireOp",EDGE,"E13.2.63.0"),sQuery(id+"F0.wireOp",EDGE,"E13.3.63.0"),sQuery(id+"F0.wireOp",EDGE,"E13.6.63.0"),sQuery(id+"F0.wireOp",EDGE,"E13.2.64.0"),sQuery(id+"F0.wireOp",EDGE,"E13.3.64.0"),sQuery(id+"F0.wireOp",EDGE,"E13.6.64.0"),sQuery(id+"F0.wireOp",EDGE,"E13.2.65.0"),sQuery(id+"F0.wireOp",EDGE,"E13.3.65.0"),sQuery(id+"F0.wireOp",EDGE,"E13.6.65.0"),sQuery(id+"F0.wireOp",EDGE,"E13.2.66.0"),sQuery(id+"F0.wireOp",EDGE,"E13.3.66.0"),sQuery(id+"F0.wireOp",EDGE,"E13.6.66.0"),sQuery(id+"F0.wireOp",EDGE,"E13.2.67.0"),sQuery(id+"F0.wireOp",EDGE,"E13.3.67.0"),sQuery(id+"F0.wireOp",EDGE,"E13.6.67.0"),sQuery(id+"F0.wireOp",EDGE,"E13.2.68.0"),sQuery(id+"F0.wireOp",EDGE,"E13.3.68.0"),sQuery(id+"F0.wireOp",EDGE,"E13.6.68.0"),sQuery(id+"F0.wireOp",EDGE,"E13.2.69.0"),sQuery(id+"F0.wireOp",EDGE,"E13.3.69.0"),sQuery(id+"F0.wireOp",EDGE,"E13.6.69.0"),sQuery(id+"F0.wireOp",EDGE,"E13.2.70.0"),sQuery(id+"F0.wireOp",EDGE,"E13.3.70.0"),sQuery(id+"F0.wireOp",EDGE,"E13.6.70.0"),sQuery(id+"F0.wireOp",EDGE,"E13.2.71.0"),sQuery(id+"F0.wireOp",EDGE,"E13.3.71.0"),sQuery(id+"F0.wireOp",EDGE,"E13.6.71.0"),sQuery(id+"F0.wireOp",EDGE,"E13.2.72.0"),sQuery(id+"F0.wireOp",EDGE,"E13.3.72.0"),sQuery(id+"F0.wireOp",EDGE,"E13.6.72.0"),sQuery(id+"F0.wireOp",EDGE,"E13.2.73.0"),sQuery(id+"F0.wireOp",EDGE,"E13.3.73.0"),sQuery(id+"F0.wireOp",EDGE,"E13.6.73.0"),sQuery(id+"F0.wireOp",EDGE,"E13.2.74.0"),sQuery(id+"F0.wireOp",EDGE,"E13.3.74.0"),sQuery(id+"F0.wireOp",EDGE,"E13.6.74.0"),sQuery(id+"F0.wireOp",EDGE,"E13.2.75.0"),sQuery(id+"F0.wireOp",EDGE,"E13.3.75.0"),sQuery(id+"F0.wireOp",EDGE,"E13.6.75.0"),sQuery(id+"F0.wireOp",EDGE,"E13.2.76.0"),sQuery(id+"F0.wireOp",EDGE,"E13.3.76.0"),sQuery(id+"F0.wireOp",EDGE,"E13.6.76.0"),sQuery(id+"F0.wireOp",EDGE,"E13.2.77.0"),sQuery(id+"F0.wireOp",EDGE,"E13.3.77.0"),sQuery(id+"F0.wireOp",EDGE,"E13.6.77.0"),sQuery(id+"F0.wireOp",EDGE,"E13.2.78.0"),sQuery(id+"F0.wireOp",EDGE,"E13.3.78.0"),sQuery(id+"F0.wireOp",EDGE,"E13.6.78.0"),sQuery(id+"F0.wireOp",EDGE,"E13.2.79.0"),sQuery(id+"F0.wireOp",EDGE,"E13.3.79.0"),sQuery(id+"F0.wireOp",EDGE,"E13.6.79.0"),sQuery(id+"F0.wireOp",EDGE,"E13.2.80.0"),sQuery(id+"F0.wireOp",EDGE,"E13.3.80.0"),sQuery(id+"F0.wireOp",EDGE,"E13.6.80.0"),sQuery(id+"F0.wireOp",EDGE,"E13.2.81.0"),sQuery(id+"F0.wireOp",EDGE,"E13.3.81.0"),sQuery(id+"F0.wireOp",EDGE,"E13.6.81.0"),sQuery(id+"F0.wireOp",EDGE,"E13.2.82.0"),sQuery(id+"F0.wireOp",EDGE,"E13.3.82.0"),sQuery(id+"F0.wireOp",EDGE,"E13.6.82.0"),sQuery(id+"F0.wireOp",EDGE,"E13.2.83.0"),sQuery(id+"F0.wireOp",EDGE,"E13.3.83.0"),sQuery(id+"F0.wireOp",EDGE,"E13.6.83.0"),sQuery(id+"F0.wireOp",EDGE,"E13.2.84.0"),sQuery(id+"F0.wireOp",EDGE,"E13.3.84.0"),sQuery(id+"F0.wireOp",EDGE,"E13.6.84.0"),sQuery(id+"F0.wireOp",EDGE,"E13.2.85.0"),sQuery(id+"F0.wireOp",EDGE,"E13.3.85.0"),sQuery(id+"F0.wireOp",EDGE,"E13.6.85.0"),sQuery(id+"F0.wireOp",EDGE,"E13.2.86.0"),sQuery(id+"F0.wireOp",EDGE,"E13.3.86.0"),sQuery(id+"F0.wireOp",EDGE,"E13.6.86.0"),sQuery(id+"F0.wireOp",EDGE,"E13.2.87.0"),sQuery(id+"F0.wireOp",EDGE,"E13.3.87.0"),sQuery(id+"F0.wireOp",EDGE,"E13.6.87.0"),sQuery(id+"F0.wireOp",EDGE,"E13.2.88.0"),sQuery(id+"F0.wireOp",EDGE,"E13.3.88.0"),sQuery(id+"F0.wireOp",EDGE,"E13.6.88.0"),sQuery(id+"F0.wireOp",EDGE,"E13.2.89.0"),sQuery(id+"F0.wireOp",EDGE,"E13.3.89.0"),sQuery(id+"F0.wireOp",EDGE,"E13.6.89.0"),sQuery(id+"F0.wireOp",EDGE,"E13.2.90.0"),sQuery(id+"F0.wireOp",EDGE,"E13.3.90.0"),sQuery(id+"F0.wireOp",EDGE,"E13.6.90.0"),sQuery(id+"F0.wireOp",EDGE,"E13.2.91.0"),sQuery(id+"F0.wireOp",EDGE,"E13.3.91.0"),sQuery(id+"F0.wireOp",EDGE,"E13.6.91.0"),sQuery(id+"F0.wireOp",EDGE,"E13.2.92.0"),sQuery(id+"F0.wireOp",EDGE,"E13.3.92.0"),sQuery(id+"F0.wireOp",EDGE,"E13.6.92.0"),sQuery(id+"F0.wireOp",EDGE,"E13.2.93.0"),sQuery(id+"F0.wireOp",EDGE,"E13.3.93.0"),sQuery(id+"F0.wireOp",EDGE,"E13.6.93.0"),sQuery(id+"F0.wireOp",EDGE,"E13.2.94.0"),sQuery(id+"F0.wireOp",EDGE,"E13.3.94.0"),sQuery(id+"F0.wireOp",EDGE,"E13.6.94.0"),sQuery(id+"F0.wireOp",EDGE,"E13.2.95.0"),sQuery(id+"F0.wireOp",EDGE,"E13.3.95.0"),sQuery(id+"F0.wireOp",EDGE,"E13.6.95.0"),sQuery(id+"F0.wireOp",EDGE,"E13.2.96.0"),sQuery(id+"F0.wireOp",EDGE,"E13.3.96.0"),sQuery(id+"F0.wireOp",EDGE,"E13.6.96.0"),sQuery(id+"F0.wireOp",EDGE,"E13.2.97.0"),sQuery(id+"F0.wireOp",EDGE,"E13.3.97.0"),sQuery(id+"F0.wireOp",EDGE,"E13.6.97.0"),sQuery(id+"F0.wireOp",EDGE,"E13.2.98.0"),sQuery(id+"F0.wireOp",EDGE,"E13.3.98.0"),sQuery(id+"F0.wireOp",EDGE,"E13.6.98.0"),sQuery(id+"F0.wireOp",EDGE,"E13.2.99.0"),sQuery(id+"F0.wireOp",EDGE,"E13.3.99.0"),sQuery(id+"F0.wireOp",EDGE,"E13.6.99.0"),sQuery(id+"F0.wireOp",EDGE,"E13.2.100.0"),sQuery(id+"F0.wireOp",EDGE,"E13.3.100.0"),sQuery(id+"F0.wireOp",EDGE,"E13.6.100.0"),sQuery(id+"F0.wireOp",EDGE,"E13.2.101.0"),sQuery(id+"F0.wireOp",EDGE,"E13.3.101.0"),sQuery(id+"F0.wireOp",EDGE,"E13.6.101.0"),sQuery(id+"F0.wireOp",EDGE,"E13.2.102.0"),sQuery(id+"F0.wireOp",EDGE,"E13.3.102.0"),sQuery(id+"F0.wireOp",EDGE,"E13.6.102.0"),sQuery(id+"F0.wireOp",EDGE,"E13.2.103.0"),sQuery(id+"F0.wireOp",EDGE,"E13.3.103.0"),sQuery(id+"F0.wireOp",EDGE,"E13.6.103.0"),sQuery(id+"F0.wireOp",EDGE,"E13.2.104.0"),sQuery(id+"F0.wireOp",EDGE,"E13.3.104.0"),sQuery(id+"F0.wireOp",EDGE,"E13.6.104.0"),sQuery(id+"F0.wireOp",EDGE,"E13.2.105.0"),sQuery(id+"F0.wireOp",EDGE,"E13.3.105.0"),sQuery(id+"F0.wireOp",EDGE,"E13.6.105.0"),sQuery(id+"F0.wireOp",EDGE,"E13.2.106.0"),sQuery(id+"F0.wireOp",EDGE,"E13.3.106.0"),sQuery(id+"F0.wireOp",EDGE,"E13.6.106.0"),sQuery(id+"F0.wireOp",EDGE,"E13.2.107.0"),sQuery(id+"F0.wireOp",EDGE,"E13.3.107.0"),sQuery(id+"F0.wireOp",EDGE,"E13.6.107.0"),sQuery(id+"F0.wireOp",EDGE,"E13.2.108.0"),sQuery(id+"F0.wireOp",EDGE,"E13.3.108.0"),sQuery(id+"F0.wireOp",EDGE,"E13.6.108.0"),sQuery(id+"F0.wireOp",EDGE,"E13.2.109.0"),sQuery(id+"F0.wireOp",EDGE,"E13.3.109.0"),sQuery(id+"F0.wireOp",EDGE,"E13.6.109.0"),sQuery(id+"F0.wireOp",EDGE,"E13.2.110.0"),sQuery(id+"F0.wireOp",EDGE,"E13.3.110.0"),sQuery(id+"F0.wireOp",EDGE,"E13.6.110.0"),sQuery(id+"F0.wireOp",EDGE,"E13.2.111.0"),sQuery(id+"F0.wireOp",EDGE,"E13.3.111.0"),sQuery(id+"F0.wireOp",EDGE,"E13.6.111.0"),sQuery(id+"F0.wireOp",EDGE,"E13.2.112.0"),sQuery(id+"F0.wireOp",EDGE,"E13.3.112.0"),sQuery(id+"F0.wireOp",EDGE,"E13.6.112.0"),sQuery(id+"F0.wireOp",EDGE,"E13.2.113.0"),sQuery(id+"F0.wireOp",EDGE,"E13.3.113.0"),sQuery(id+"F0.wireOp",EDGE,"E13.6.113.0"),sQuery(id+"F0.wireOp",EDGE,"E13.2.114.0"),sQuery(id+"F0.wireOp",EDGE,"E13.3.114.0"),sQuery(id+"F0.wireOp",EDGE,"E13.6.114.0"),sQuery(id+"F0.wireOp",EDGE,"E13.2.115.0"),sQuery(id+"F0.wireOp",EDGE,"E13.3.115.0"),sQuery(id+"F0.wireOp",EDGE,"E13.6.115.0"),sQuery(id+"F0.wireOp",EDGE,"E13.2.116.0"),sQuery(id+"F0.wireOp",EDGE,"E13.3.116.0"),sQuery(id+"F0.wireOp",EDGE,"E13.6.116.0"),sQuery(id+"F0.wireOp",EDGE,"E13.2.117.0"),sQuery(id+"F0.wireOp",EDGE,"E13.3.117.0"),sQuery(id+"F0.wireOp",EDGE,"E13.6.117.0"),sQuery(id+"F0.wireOp",EDGE,"E13.2.118.0"),sQuery(id+"F0.wireOp",EDGE,"E13.3.118.0"),sQuery(id+"F0.wireOp",EDGE,"E13.6.118.0"),sQuery(id+"F0.wireOp",EDGE,"E13.2.119.0"),sQuery(id+"F0.wireOp",EDGE,"E13.3.119.0"),sQuery(id+"F0.wireOp",EDGE,"E13.6.119.0"),sQuery(id+"F0.wireOp",EDGE,"E14")])],"isStart":false});
            var sketch = newSketch(context, id + "F2", { "sketchPlane" : qUnion([Q0])});
            skLineSegment(sketch, "E15.bottom", {"start": v(-55, 55) * mm, "end": v(55, 55) * mm, "construction": true});
            skLineSegment(sketch, "E15.top", {"start": v(-55, -55) * mm, "end": v(55, -55) * mm, "construction": true});
            skLineSegment(sketch, "E15.left", {"start": v(-55, 55) * mm, "end": v(-55, -55) * mm, "construction": true});
            skLineSegment(sketch, "E15.right", {"start": v(55, 55) * mm, "end": v(55, -55) * mm, "construction": true});
            skPoint(sketch, "E15.middle", {"position": v(0, 0) * mm});
            skCircle(sketch, "E16", {"center": v(-55, 55) * mm, "radius": 1.5 * mm});
            skCircle(sketch, "E17", {"center": v(55, 55) * mm, "radius": 1.5 * mm});
            skCircle(sketch, "E18", {"center": v(-55, -55) * mm, "radius": 1.5 * mm});
            skCircle(sketch, "E19", {"center": v(55, -55) * mm, "radius": 1.5 * mm});
            skLineSegment(sketch, "E20.bottom", {"start": v(45, 45) * mm, "end": v(-45, 45) * mm, "construction": true});
            skLineSegment(sketch, "E20.top", {"start": v(45, -45) * mm, "end": v(-45, -45) * mm, "construction": true});
            skLineSegment(sketch, "E20.left", {"start": v(45, 45) * mm, "end": v(45, -45) * mm, "construction": true});
            skLineSegment(sketch, "E20.right", {"start": v(-45, 45) * mm, "end": v(-45, -45) * mm, "construction": true});
            skCircle(sketch, "E21", {"center": v(-45, 45) * mm, "radius": 1.5 * mm});
            skCircle(sketch, "E22.MirrorC", {"center": v(45, 45) * mm, "radius": 1.5 * mm});
            skCircle(sketch, "E23.MirrorC", {"center": v(-45, -45) * mm, "radius": 1.5 * mm});
            skCircle(sketch, "E24.MirrorC", {"center": v(45, -45) * mm, "radius": 1.5 * mm});
            skSolve(sketch);
        }
        {
            var Q0;
            Q0=qSketchRegion(id+"F2",true);
            var Q1;
            Q1=makeQuery(id+"F1.opExtrude","CAP_FACE",FACE,{"disambiguationData":[OSD([sQuery(id+"F0.wireOp",EDGE,"E2"),sQuery(id+"F0.wireOp",EDGE,"E7"),sQuery(id+"F0.wireOp",EDGE,"E8"),sQuery(id+"F0.wireOp",EDGE,"E9.MirrorCS"),sQuery(id+"F0.wireOp",EDGE,"E10.1.0"),sQuery(id+"F0.wireOp",EDGE,"E10.1.1"),sQuery(id+"F0.wireOp",EDGE,"E10.1.2"),sQuery(id+"F0.wireOp",EDGE,"E10.2.0"),sQuery(id+"F0.wireOp",EDGE,"E10.2.1"),sQuery(id+"F0.wireOp",EDGE,"E10.2.2"),sQuery(id+"F0.wireOp",EDGE,"E10.3.0"),sQuery(id+"F0.wireOp",EDGE,"E10.3.1"),sQuery(id+"F0.wireOp",EDGE,"E10.3.2"),sQuery(id+"F0.wireOp",EDGE,"E10.4.0"),sQuery(id+"F0.wireOp",EDGE,"E10.4.1"),sQuery(id+"F0.wireOp",EDGE,"E10.4.2"),sQuery(id+"F0.wireOp",EDGE,"E10.5.0"),sQuery(id+"F0.wireOp",EDGE,"E10.5.1"),sQuery(id+"F0.wireOp",EDGE,"E10.5.2"),sQuery(id+"F0.wireOp",EDGE,"E10.6.0"),sQuery(id+"F0.wireOp",EDGE,"E10.6.1"),sQuery(id+"F0.wireOp",EDGE,"E10.6.2"),sQuery(id+"F0.wireOp",EDGE,"E10.7.0"),sQuery(id+"F0.wireOp",EDGE,"E10.7.1"),sQuery(id+"F0.wireOp",EDGE,"E10.7.2"),sQuery(id+"F0.wireOp",EDGE,"E10.8.0"),sQuery(id+"F0.wireOp",EDGE,"E10.8.1"),sQuery(id+"F0.wireOp",EDGE,"E10.8.2"),sQuery(id+"F0.wireOp",EDGE,"E10.9.0"),sQuery(id+"F0.wireOp",EDGE,"E10.9.1"),sQuery(id+"F0.wireOp",EDGE,"E10.9.2"),sQuery(id+"F0.wireOp",EDGE,"E12.2.10.0"),sQuery(id+"F0.wireOp",EDGE,"E12.3.10.0"),sQuery(id+"F0.wireOp",EDGE,"E12.6.10.0"),sQuery(id+"F0.wireOp",EDGE,"E12.2.11.0"),sQuery(id+"F0.wireOp",EDGE,"E12.3.11.0"),sQuery(id+"F0.wireOp",EDGE,"E12.6.11.0"),sQuery(id+"F0.wireOp",EDGE,"E12.2.12.0"),sQuery(id+"F0.wireOp",EDGE,"E12.3.12.0"),sQuery(id+"F0.wireOp",EDGE,"E12.6.12.0"),sQuery(id+"F0.wireOp",EDGE,"E12.2.13.0"),sQuery(id+"F0.wireOp",EDGE,"E12.3.13.0"),sQuery(id+"F0.wireOp",EDGE,"E12.6.13.0"),sQuery(id+"F0.wireOp",EDGE,"E12.2.14.0"),sQuery(id+"F0.wireOp",EDGE,"E12.3.14.0"),sQuery(id+"F0.wireOp",EDGE,"E12.6.14.0"),sQuery(id+"F0.wireOp",EDGE,"E12.2.15.0"),sQuery(id+"F0.wireOp",EDGE,"E12.3.15.0"),sQuery(id+"F0.wireOp",EDGE,"E12.6.15.0"),sQuery(id+"F0.wireOp",EDGE,"E12.2.16.0"),sQuery(id+"F0.wireOp",EDGE,"E12.3.16.0"),sQuery(id+"F0.wireOp",EDGE,"E12.6.16.0"),sQuery(id+"F0.wireOp",EDGE,"E12.2.17.0"),sQuery(id+"F0.wireOp",EDGE,"E12.3.17.0"),sQuery(id+"F0.wireOp",EDGE,"E12.6.17.0"),sQuery(id+"F0.wireOp",EDGE,"E12.2.18.0"),sQuery(id+"F0.wireOp",EDGE,"E12.3.18.0"),sQuery(id+"F0.wireOp",EDGE,"E12.6.18.0"),sQuery(id+"F0.wireOp",EDGE,"E12.2.19.0"),sQuery(id+"F0.wireOp",EDGE,"E12.3.19.0"),sQuery(id+"F0.wireOp",EDGE,"E12.6.19.0"),sQuery(id+"F0.wireOp",EDGE,"E12.2.20.0"),sQuery(id+"F0.wireOp",EDGE,"E12.3.20.0"),sQuery(id+"F0.wireOp",EDGE,"E12.6.20.0"),sQuery(id+"F0.wireOp",EDGE,"E12.2.21.0"),sQuery(id+"F0.wireOp",EDGE,"E12.3.21.0"),sQuery(id+"F0.wireOp",EDGE,"E12.6.21.0"),sQuery(id+"F0.wireOp",EDGE,"E12.2.22.0"),sQuery(id+"F0.wireOp",EDGE,"E12.3.22.0"),sQuery(id+"F0.wireOp",EDGE,"E12.6.22.0"),sQuery(id+"F0.wireOp",EDGE,"E12.2.23.0"),sQuery(id+"F0.wireOp",EDGE,"E12.3.23.0"),sQuery(id+"F0.wireOp",EDGE,"E12.6.23.0"),sQuery(id+"F0.wireOp",EDGE,"E12.2.24.0"),sQuery(id+"F0.wireOp",EDGE,"E12.3.24.0"),sQuery(id+"F0.wireOp",EDGE,"E12.6.24.0"),sQuery(id+"F0.wireOp",EDGE,"E12.2.25.0"),sQuery(id+"F0.wireOp",EDGE,"E12.3.25.0"),sQuery(id+"F0.wireOp",EDGE,"E12.6.25.0"),sQuery(id+"F0.wireOp",EDGE,"E12.2.26.0"),sQuery(id+"F0.wireOp",EDGE,"E12.3.26.0"),sQuery(id+"F0.wireOp",EDGE,"E12.6.26.0"),sQuery(id+"F0.wireOp",EDGE,"E12.2.27.0"),sQuery(id+"F0.wireOp",EDGE,"E12.3.27.0"),sQuery(id+"F0.wireOp",EDGE,"E12.6.27.0"),sQuery(id+"F0.wireOp",EDGE,"E12.2.28.0"),sQuery(id+"F0.wireOp",EDGE,"E12.3.28.0"),sQuery(id+"F0.wireOp",EDGE,"E12.6.28.0"),sQuery(id+"F0.wireOp",EDGE,"E12.2.29.0"),sQuery(id+"F0.wireOp",EDGE,"E12.3.29.0"),sQuery(id+"F0.wireOp",EDGE,"E12.6.29.0"),sQuery(id+"F0.wireOp",EDGE,"E12.2.30.0"),sQuery(id+"F0.wireOp",EDGE,"E12.3.30.0"),sQuery(id+"F0.wireOp",EDGE,"E12.6.30.0"),sQuery(id+"F0.wireOp",EDGE,"E12.2.31.0"),sQuery(id+"F0.wireOp",EDGE,"E12.3.31.0"),sQuery(id+"F0.wireOp",EDGE,"E12.6.31.0"),sQuery(id+"F0.wireOp",EDGE,"E12.2.32.0"),sQuery(id+"F0.wireOp",EDGE,"E12.3.32.0"),sQuery(id+"F0.wireOp",EDGE,"E12.6.32.0"),sQuery(id+"F0.wireOp",EDGE,"E12.2.33.0"),sQuery(id+"F0.wireOp",EDGE,"E12.3.33.0"),sQuery(id+"F0.wireOp",EDGE,"E12.6.33.0"),sQuery(id+"F0.wireOp",EDGE,"E12.2.34.0"),sQuery(id+"F0.wireOp",EDGE,"E12.3.34.0"),sQuery(id+"F0.wireOp",EDGE,"E12.6.34.0"),sQuery(id+"F0.wireOp",EDGE,"E12.2.35.0"),sQuery(id+"F0.wireOp",EDGE,"E12.3.35.0"),sQuery(id+"F0.wireOp",EDGE,"E12.6.35.0"),sQuery(id+"F0.wireOp",EDGE,"E12.2.36.0"),sQuery(id+"F0.wireOp",EDGE,"E12.3.36.0"),sQuery(id+"F0.wireOp",EDGE,"E12.6.36.0"),sQuery(id+"F0.wireOp",EDGE,"E12.2.37.0"),sQuery(id+"F0.wireOp",EDGE,"E12.3.37.0"),sQuery(id+"F0.wireOp",EDGE,"E12.6.37.0"),sQuery(id+"F0.wireOp",EDGE,"E12.2.38.0"),sQuery(id+"F0.wireOp",EDGE,"E12.3.38.0"),sQuery(id+"F0.wireOp",EDGE,"E12.6.38.0"),sQuery(id+"F0.wireOp",EDGE,"E12.2.39.0"),sQuery(id+"F0.wireOp",EDGE,"E12.3.39.0"),sQuery(id+"F0.wireOp",EDGE,"E12.6.39.0"),sQuery(id+"F0.wireOp",EDGE,"E12.2.40.0"),sQuery(id+"F0.wireOp",EDGE,"E12.3.40.0"),sQuery(id+"F0.wireOp",EDGE,"E12.6.40.0"),sQuery(id+"F0.wireOp",EDGE,"E12.2.41.0"),sQuery(id+"F0.wireOp",EDGE,"E12.3.41.0"),sQuery(id+"F0.wireOp",EDGE,"E12.6.41.0"),sQuery(id+"F0.wireOp",EDGE,"E12.2.42.0"),sQuery(id+"F0.wireOp",EDGE,"E12.3.42.0"),sQuery(id+"F0.wireOp",EDGE,"E12.6.42.0"),sQuery(id+"F0.wireOp",EDGE,"E12.2.43.0"),sQuery(id+"F0.wireOp",EDGE,"E12.3.43.0"),sQuery(id+"F0.wireOp",EDGE,"E12.6.43.0"),sQuery(id+"F0.wireOp",EDGE,"E12.2.44.0"),sQuery(id+"F0.wireOp",EDGE,"E12.3.44.0"),sQuery(id+"F0.wireOp",EDGE,"E12.6.44.0"),sQuery(id+"F0.wireOp",EDGE,"E12.2.45.0"),sQuery(id+"F0.wireOp",EDGE,"E12.3.45.0"),sQuery(id+"F0.wireOp",EDGE,"E12.6.45.0"),sQuery(id+"F0.wireOp",EDGE,"E12.2.46.0"),sQuery(id+"F0.wireOp",EDGE,"E12.3.46.0"),sQuery(id+"F0.wireOp",EDGE,"E12.6.46.0"),sQuery(id+"F0.wireOp",EDGE,"E12.2.47.0"),sQuery(id+"F0.wireOp",EDGE,"E12.3.47.0"),sQuery(id+"F0.wireOp",EDGE,"E12.6.47.0"),sQuery(id+"F0.wireOp",EDGE,"E12.2.48.0"),sQuery(id+"F0.wireOp",EDGE,"E12.3.48.0"),sQuery(id+"F0.wireOp",EDGE,"E12.6.48.0"),sQuery(id+"F0.wireOp",EDGE,"E12.2.49.0"),sQuery(id+"F0.wireOp",EDGE,"E12.3.49.0"),sQuery(id+"F0.wireOp",EDGE,"E12.6.49.0"),sQuery(id+"F0.wireOp",EDGE,"E12.2.50.0"),sQuery(id+"F0.wireOp",EDGE,"E12.3.50.0"),sQuery(id+"F0.wireOp",EDGE,"E12.6.50.0"),sQuery(id+"F0.wireOp",EDGE,"E12.2.51.0"),sQuery(id+"F0.wireOp",EDGE,"E12.3.51.0"),sQuery(id+"F0.wireOp",EDGE,"E12.6.51.0"),sQuery(id+"F0.wireOp",EDGE,"E12.2.52.0"),sQuery(id+"F0.wireOp",EDGE,"E12.3.52.0"),sQuery(id+"F0.wireOp",EDGE,"E12.6.52.0"),sQuery(id+"F0.wireOp",EDGE,"E12.2.53.0"),sQuery(id+"F0.wireOp",EDGE,"E12.3.53.0"),sQuery(id+"F0.wireOp",EDGE,"E12.6.53.0"),sQuery(id+"F0.wireOp",EDGE,"E12.2.54.0"),sQuery(id+"F0.wireOp",EDGE,"E12.3.54.0"),sQuery(id+"F0.wireOp",EDGE,"E12.6.54.0"),sQuery(id+"F0.wireOp",EDGE,"E12.2.55.0"),sQuery(id+"F0.wireOp",EDGE,"E12.3.55.0"),sQuery(id+"F0.wireOp",EDGE,"E12.6.55.0"),sQuery(id+"F0.wireOp",EDGE,"E12.2.56.0"),sQuery(id+"F0.wireOp",EDGE,"E12.3.56.0"),sQuery(id+"F0.wireOp",EDGE,"E12.6.56.0"),sQuery(id+"F0.wireOp",EDGE,"E12.2.57.0"),sQuery(id+"F0.wireOp",EDGE,"E12.3.57.0"),sQuery(id+"F0.wireOp",EDGE,"E12.6.57.0"),sQuery(id+"F0.wireOp",EDGE,"E12.2.58.0"),sQuery(id+"F0.wireOp",EDGE,"E12.3.58.0"),sQuery(id+"F0.wireOp",EDGE,"E12.6.58.0"),sQuery(id+"F0.wireOp",EDGE,"E12.2.59.0"),sQuery(id+"F0.wireOp",EDGE,"E12.3.59.0"),sQuery(id+"F0.wireOp",EDGE,"E12.6.59.0"),sQuery(id+"F0.wireOp",EDGE,"E13.2.60.0"),sQuery(id+"F0.wireOp",EDGE,"E13.3.60.0"),sQuery(id+"F0.wireOp",EDGE,"E13.6.60.0"),sQuery(id+"F0.wireOp",EDGE,"E13.2.61.0"),sQuery(id+"F0.wireOp",EDGE,"E13.3.61.0"),sQuery(id+"F0.wireOp",EDGE,"E13.6.61.0"),sQuery(id+"F0.wireOp",EDGE,"E13.2.62.0"),sQuery(id+"F0.wireOp",EDGE,"E13.3.62.0"),sQuery(id+"F0.wireOp",EDGE,"E13.6.62.0"),sQuery(id+"F0.wireOp",EDGE,"E13.2.63.0"),sQuery(id+"F0.wireOp",EDGE,"E13.3.63.0"),sQuery(id+"F0.wireOp",EDGE,"E13.6.63.0"),sQuery(id+"F0.wireOp",EDGE,"E13.2.64.0"),sQuery(id+"F0.wireOp",EDGE,"E13.3.64.0"),sQuery(id+"F0.wireOp",EDGE,"E13.6.64.0"),sQuery(id+"F0.wireOp",EDGE,"E13.2.65.0"),sQuery(id+"F0.wireOp",EDGE,"E13.3.65.0"),sQuery(id+"F0.wireOp",EDGE,"E13.6.65.0"),sQuery(id+"F0.wireOp",EDGE,"E13.2.66.0"),sQuery(id+"F0.wireOp",EDGE,"E13.3.66.0"),sQuery(id+"F0.wireOp",EDGE,"E13.6.66.0"),sQuery(id+"F0.wireOp",EDGE,"E13.2.67.0"),sQuery(id+"F0.wireOp",EDGE,"E13.3.67.0"),sQuery(id+"F0.wireOp",EDGE,"E13.6.67.0"),sQuery(id+"F0.wireOp",EDGE,"E13.2.68.0"),sQuery(id+"F0.wireOp",EDGE,"E13.3.68.0"),sQuery(id+"F0.wireOp",EDGE,"E13.6.68.0"),sQuery(id+"F0.wireOp",EDGE,"E13.2.69.0"),sQuery(id+"F0.wireOp",EDGE,"E13.3.69.0"),sQuery(id+"F0.wireOp",EDGE,"E13.6.69.0"),sQuery(id+"F0.wireOp",EDGE,"E13.2.70.0"),sQuery(id+"F0.wireOp",EDGE,"E13.3.70.0"),sQuery(id+"F0.wireOp",EDGE,"E13.6.70.0"),sQuery(id+"F0.wireOp",EDGE,"E13.2.71.0"),sQuery(id+"F0.wireOp",EDGE,"E13.3.71.0"),sQuery(id+"F0.wireOp",EDGE,"E13.6.71.0"),sQuery(id+"F0.wireOp",EDGE,"E13.2.72.0"),sQuery(id+"F0.wireOp",EDGE,"E13.3.72.0"),sQuery(id+"F0.wireOp",EDGE,"E13.6.72.0"),sQuery(id+"F0.wireOp",EDGE,"E13.2.73.0"),sQuery(id+"F0.wireOp",EDGE,"E13.3.73.0"),sQuery(id+"F0.wireOp",EDGE,"E13.6.73.0"),sQuery(id+"F0.wireOp",EDGE,"E13.2.74.0"),sQuery(id+"F0.wireOp",EDGE,"E13.3.74.0"),sQuery(id+"F0.wireOp",EDGE,"E13.6.74.0"),sQuery(id+"F0.wireOp",EDGE,"E13.2.75.0"),sQuery(id+"F0.wireOp",EDGE,"E13.3.75.0"),sQuery(id+"F0.wireOp",EDGE,"E13.6.75.0"),sQuery(id+"F0.wireOp",EDGE,"E13.2.76.0"),sQuery(id+"F0.wireOp",EDGE,"E13.3.76.0"),sQuery(id+"F0.wireOp",EDGE,"E13.6.76.0"),sQuery(id+"F0.wireOp",EDGE,"E13.2.77.0"),sQuery(id+"F0.wireOp",EDGE,"E13.3.77.0"),sQuery(id+"F0.wireOp",EDGE,"E13.6.77.0"),sQuery(id+"F0.wireOp",EDGE,"E13.2.78.0"),sQuery(id+"F0.wireOp",EDGE,"E13.3.78.0"),sQuery(id+"F0.wireOp",EDGE,"E13.6.78.0"),sQuery(id+"F0.wireOp",EDGE,"E13.2.79.0"),sQuery(id+"F0.wireOp",EDGE,"E13.3.79.0"),sQuery(id+"F0.wireOp",EDGE,"E13.6.79.0"),sQuery(id+"F0.wireOp",EDGE,"E13.2.80.0"),sQuery(id+"F0.wireOp",EDGE,"E13.3.80.0"),sQuery(id+"F0.wireOp",EDGE,"E13.6.80.0"),sQuery(id+"F0.wireOp",EDGE,"E13.2.81.0"),sQuery(id+"F0.wireOp",EDGE,"E13.3.81.0"),sQuery(id+"F0.wireOp",EDGE,"E13.6.81.0"),sQuery(id+"F0.wireOp",EDGE,"E13.2.82.0"),sQuery(id+"F0.wireOp",EDGE,"E13.3.82.0"),sQuery(id+"F0.wireOp",EDGE,"E13.6.82.0"),sQuery(id+"F0.wireOp",EDGE,"E13.2.83.0"),sQuery(id+"F0.wireOp",EDGE,"E13.3.83.0"),sQuery(id+"F0.wireOp",EDGE,"E13.6.83.0"),sQuery(id+"F0.wireOp",EDGE,"E13.2.84.0"),sQuery(id+"F0.wireOp",EDGE,"E13.3.84.0"),sQuery(id+"F0.wireOp",EDGE,"E13.6.84.0"),sQuery(id+"F0.wireOp",EDGE,"E13.2.85.0"),sQuery(id+"F0.wireOp",EDGE,"E13.3.85.0"),sQuery(id+"F0.wireOp",EDGE,"E13.6.85.0"),sQuery(id+"F0.wireOp",EDGE,"E13.2.86.0"),sQuery(id+"F0.wireOp",EDGE,"E13.3.86.0"),sQuery(id+"F0.wireOp",EDGE,"E13.6.86.0"),sQuery(id+"F0.wireOp",EDGE,"E13.2.87.0"),sQuery(id+"F0.wireOp",EDGE,"E13.3.87.0"),sQuery(id+"F0.wireOp",EDGE,"E13.6.87.0"),sQuery(id+"F0.wireOp",EDGE,"E13.2.88.0"),sQuery(id+"F0.wireOp",EDGE,"E13.3.88.0"),sQuery(id+"F0.wireOp",EDGE,"E13.6.88.0"),sQuery(id+"F0.wireOp",EDGE,"E13.2.89.0"),sQuery(id+"F0.wireOp",EDGE,"E13.3.89.0"),sQuery(id+"F0.wireOp",EDGE,"E13.6.89.0"),sQuery(id+"F0.wireOp",EDGE,"E13.2.90.0"),sQuery(id+"F0.wireOp",EDGE,"E13.3.90.0"),sQuery(id+"F0.wireOp",EDGE,"E13.6.90.0"),sQuery(id+"F0.wireOp",EDGE,"E13.2.91.0"),sQuery(id+"F0.wireOp",EDGE,"E13.3.91.0"),sQuery(id+"F0.wireOp",EDGE,"E13.6.91.0"),sQuery(id+"F0.wireOp",EDGE,"E13.2.92.0"),sQuery(id+"F0.wireOp",EDGE,"E13.3.92.0"),sQuery(id+"F0.wireOp",EDGE,"E13.6.92.0"),sQuery(id+"F0.wireOp",EDGE,"E13.2.93.0"),sQuery(id+"F0.wireOp",EDGE,"E13.3.93.0"),sQuery(id+"F0.wireOp",EDGE,"E13.6.93.0"),sQuery(id+"F0.wireOp",EDGE,"E13.2.94.0"),sQuery(id+"F0.wireOp",EDGE,"E13.3.94.0"),sQuery(id+"F0.wireOp",EDGE,"E13.6.94.0"),sQuery(id+"F0.wireOp",EDGE,"E13.2.95.0"),sQuery(id+"F0.wireOp",EDGE,"E13.3.95.0"),sQuery(id+"F0.wireOp",EDGE,"E13.6.95.0"),sQuery(id+"F0.wireOp",EDGE,"E13.2.96.0"),sQuery(id+"F0.wireOp",EDGE,"E13.3.96.0"),sQuery(id+"F0.wireOp",EDGE,"E13.6.96.0"),sQuery(id+"F0.wireOp",EDGE,"E13.2.97.0"),sQuery(id+"F0.wireOp",EDGE,"E13.3.97.0"),sQuery(id+"F0.wireOp",EDGE,"E13.6.97.0"),sQuery(id+"F0.wireOp",EDGE,"E13.2.98.0"),sQuery(id+"F0.wireOp",EDGE,"E13.3.98.0"),sQuery(id+"F0.wireOp",EDGE,"E13.6.98.0"),sQuery(id+"F0.wireOp",EDGE,"E13.2.99.0"),sQuery(id+"F0.wireOp",EDGE,"E13.3.99.0"),sQuery(id+"F0.wireOp",EDGE,"E13.6.99.0"),sQuery(id+"F0.wireOp",EDGE,"E13.2.100.0"),sQuery(id+"F0.wireOp",EDGE,"E13.3.100.0"),sQuery(id+"F0.wireOp",EDGE,"E13.6.100.0"),sQuery(id+"F0.wireOp",EDGE,"E13.2.101.0"),sQuery(id+"F0.wireOp",EDGE,"E13.3.101.0"),sQuery(id+"F0.wireOp",EDGE,"E13.6.101.0"),sQuery(id+"F0.wireOp",EDGE,"E13.2.102.0"),sQuery(id+"F0.wireOp",EDGE,"E13.3.102.0"),sQuery(id+"F0.wireOp",EDGE,"E13.6.102.0"),sQuery(id+"F0.wireOp",EDGE,"E13.2.103.0"),sQuery(id+"F0.wireOp",EDGE,"E13.3.103.0"),sQuery(id+"F0.wireOp",EDGE,"E13.6.103.0"),sQuery(id+"F0.wireOp",EDGE,"E13.2.104.0"),sQuery(id+"F0.wireOp",EDGE,"E13.3.104.0"),sQuery(id+"F0.wireOp",EDGE,"E13.6.104.0"),sQuery(id+"F0.wireOp",EDGE,"E13.2.105.0"),sQuery(id+"F0.wireOp",EDGE,"E13.3.105.0"),sQuery(id+"F0.wireOp",EDGE,"E13.6.105.0"),sQuery(id+"F0.wireOp",EDGE,"E13.2.106.0"),sQuery(id+"F0.wireOp",EDGE,"E13.3.106.0"),sQuery(id+"F0.wireOp",EDGE,"E13.6.106.0"),sQuery(id+"F0.wireOp",EDGE,"E13.2.107.0"),sQuery(id+"F0.wireOp",EDGE,"E13.3.107.0"),sQuery(id+"F0.wireOp",EDGE,"E13.6.107.0"),sQuery(id+"F0.wireOp",EDGE,"E13.2.108.0"),sQuery(id+"F0.wireOp",EDGE,"E13.3.108.0"),sQuery(id+"F0.wireOp",EDGE,"E13.6.108.0"),sQuery(id+"F0.wireOp",EDGE,"E13.2.109.0"),sQuery(id+"F0.wireOp",EDGE,"E13.3.109.0"),sQuery(id+"F0.wireOp",EDGE,"E13.6.109.0"),sQuery(id+"F0.wireOp",EDGE,"E13.2.110.0"),sQuery(id+"F0.wireOp",EDGE,"E13.3.110.0"),sQuery(id+"F0.wireOp",EDGE,"E13.6.110.0"),sQuery(id+"F0.wireOp",EDGE,"E13.2.111.0"),sQuery(id+"F0.wireOp",EDGE,"E13.3.111.0"),sQuery(id+"F0.wireOp",EDGE,"E13.6.111.0"),sQuery(id+"F0.wireOp",EDGE,"E13.2.112.0"),sQuery(id+"F0.wireOp",EDGE,"E13.3.112.0"),sQuery(id+"F0.wireOp",EDGE,"E13.6.112.0"),sQuery(id+"F0.wireOp",EDGE,"E13.2.113.0"),sQuery(id+"F0.wireOp",EDGE,"E13.3.113.0"),sQuery(id+"F0.wireOp",EDGE,"E13.6.113.0"),sQuery(id+"F0.wireOp",EDGE,"E13.2.114.0"),sQuery(id+"F0.wireOp",EDGE,"E13.3.114.0"),sQuery(id+"F0.wireOp",EDGE,"E13.6.114.0"),sQuery(id+"F0.wireOp",EDGE,"E13.2.115.0"),sQuery(id+"F0.wireOp",EDGE,"E13.3.115.0"),sQuery(id+"F0.wireOp",EDGE,"E13.6.115.0"),sQuery(id+"F0.wireOp",EDGE,"E13.2.116.0"),sQuery(id+"F0.wireOp",EDGE,"E13.3.116.0"),sQuery(id+"F0.wireOp",EDGE,"E13.6.116.0"),sQuery(id+"F0.wireOp",EDGE,"E13.2.117.0"),sQuery(id+"F0.wireOp",EDGE,"E13.3.117.0"),sQuery(id+"F0.wireOp",EDGE,"E13.6.117.0"),sQuery(id+"F0.wireOp",EDGE,"E13.2.118.0"),sQuery(id+"F0.wireOp",EDGE,"E13.3.118.0"),sQuery(id+"F0.wireOp",EDGE,"E13.6.118.0"),sQuery(id+"F0.wireOp",EDGE,"E13.2.119.0"),sQuery(id+"F0.wireOp",EDGE,"E13.3.119.0"),sQuery(id+"F0.wireOp",EDGE,"E13.6.119.0"),sQuery(id+"F0.wireOp",EDGE,"E14")])],"isStart":true});
            extrude(context, id + "F3", {"entities" : qUnion([Q0]), "operationType" : NewBodyOperationType.REMOVE, "oppositeDirection" : true, "endBoundEntityFace" : qUnion([Q1]), "depth" : 1 * mm, "offsetDistance" : 25 * mm});
        }
        {
            var Q0;
            Q0=qCreatedBy(makeId("Front.planeOp"),FACE);
            var sketch = newSketch(context, id + "F4", { "sketchPlane" : qUnion([Q0])});
            skCircle(sketch, "E25", {"center": v(0, 0) * mm, "radius": 100 * mm});
            skSolve(sketch);
        }
        {
            var Q0;
            Q0 = qSketchRegion(id + "F4", true);
            var Q1;
            Q1=makeQuery(id+"F1.opExtrude","CAP_FACE",FACE,{"disambiguationData":[OSD([sQuery(id+"F0.wireOp",EDGE,"E2"),sQuery(id+"F0.wireOp",EDGE,"E7"),sQuery(id+"F0.wireOp",EDGE,"E8"),sQuery(id+"F0.wireOp",EDGE,"E9.MirrorCS"),sQuery(id+"F0.wireOp",EDGE,"E10.1.0"),sQuery(id+"F0.wireOp",EDGE,"E10.1.1"),sQuery(id+"F0.wireOp",EDGE,"E10.1.2"),sQuery(id+"F0.wireOp",EDGE,"E10.2.0"),sQuery(id+"F0.wireOp",EDGE,"E10.2.1"),sQuery(id+"F0.wireOp",EDGE,"E10.2.2"),sQuery(id+"F0.wireOp",EDGE,"E10.3.0"),sQuery(id+"F0.wireOp",EDGE,"E10.3.1"),sQuery(id+"F0.wireOp",EDGE,"E10.3.2"),sQuery(id+"F0.wireOp",EDGE,"E10.4.0"),sQuery(id+"F0.wireOp",EDGE,"E10.4.1"),sQuery(id+"F0.wireOp",EDGE,"E10.4.2"),sQuery(id+"F0.wireOp",EDGE,"E10.5.0"),sQuery(id+"F0.wireOp",EDGE,"E10.5.1"),sQuery(id+"F0.wireOp",EDGE,"E10.5.2"),sQuery(id+"F0.wireOp",EDGE,"E10.6.0"),sQuery(id+"F0.wireOp",EDGE,"E10.6.1"),sQuery(id+"F0.wireOp",EDGE,"E10.6.2"),sQuery(id+"F0.wireOp",EDGE,"E10.7.0"),sQuery(id+"F0.wireOp",EDGE,"E10.7.1"),sQuery(id+"F0.wireOp",EDGE,"E10.7.2"),sQuery(id+"F0.wireOp",EDGE,"E10.8.0"),sQuery(id+"F0.wireOp",EDGE,"E10.8.1"),sQuery(id+"F0.wireOp",EDGE,"E10.8.2"),sQuery(id+"F0.wireOp",EDGE,"E10.9.0"),sQuery(id+"F0.wireOp",EDGE,"E10.9.1"),sQuery(id+"F0.wireOp",EDGE,"E10.9.2"),sQuery(id+"F0.wireOp",EDGE,"E12.2.10.0"),sQuery(id+"F0.wireOp",EDGE,"E12.3.10.0"),sQuery(id+"F0.wireOp",EDGE,"E12.6.10.0"),sQuery(id+"F0.wireOp",EDGE,"E12.2.11.0"),sQuery(id+"F0.wireOp",EDGE,"E12.3.11.0"),sQuery(id+"F0.wireOp",EDGE,"E12.6.11.0"),sQuery(id+"F0.wireOp",EDGE,"E12.2.12.0"),sQuery(id+"F0.wireOp",EDGE,"E12.3.12.0"),sQuery(id+"F0.wireOp",EDGE,"E12.6.12.0"),sQuery(id+"F0.wireOp",EDGE,"E12.2.13.0"),sQuery(id+"F0.wireOp",EDGE,"E12.3.13.0"),sQuery(id+"F0.wireOp",EDGE,"E12.6.13.0"),sQuery(id+"F0.wireOp",EDGE,"E12.2.14.0"),sQuery(id+"F0.wireOp",EDGE,"E12.3.14.0"),sQuery(id+"F0.wireOp",EDGE,"E12.6.14.0"),sQuery(id+"F0.wireOp",EDGE,"E12.2.15.0"),sQuery(id+"F0.wireOp",EDGE,"E12.3.15.0"),sQuery(id+"F0.wireOp",EDGE,"E12.6.15.0"),sQuery(id+"F0.wireOp",EDGE,"E12.2.16.0"),sQuery(id+"F0.wireOp",EDGE,"E12.3.16.0"),sQuery(id+"F0.wireOp",EDGE,"E12.6.16.0"),sQuery(id+"F0.wireOp",EDGE,"E12.2.17.0"),sQuery(id+"F0.wireOp",EDGE,"E12.3.17.0"),sQuery(id+"F0.wireOp",EDGE,"E12.6.17.0"),sQuery(id+"F0.wireOp",EDGE,"E12.2.18.0"),sQuery(id+"F0.wireOp",EDGE,"E12.3.18.0"),sQuery(id+"F0.wireOp",EDGE,"E12.6.18.0"),sQuery(id+"F0.wireOp",EDGE,"E12.2.19.0"),sQuery(id+"F0.wireOp",EDGE,"E12.3.19.0"),sQuery(id+"F0.wireOp",EDGE,"E12.6.19.0"),sQuery(id+"F0.wireOp",EDGE,"E12.2.20.0"),sQuery(id+"F0.wireOp",EDGE,"E12.3.20.0"),sQuery(id+"F0.wireOp",EDGE,"E12.6.20.0"),sQuery(id+"F0.wireOp",EDGE,"E12.2.21.0"),sQuery(id+"F0.wireOp",EDGE,"E12.3.21.0"),sQuery(id+"F0.wireOp",EDGE,"E12.6.21.0"),sQuery(id+"F0.wireOp",EDGE,"E12.2.22.0"),sQuery(id+"F0.wireOp",EDGE,"E12.3.22.0"),sQuery(id+"F0.wireOp",EDGE,"E12.6.22.0"),sQuery(id+"F0.wireOp",EDGE,"E12.2.23.0"),sQuery(id+"F0.wireOp",EDGE,"E12.3.23.0"),sQuery(id+"F0.wireOp",EDGE,"E12.6.23.0"),sQuery(id+"F0.wireOp",EDGE,"E12.2.24.0"),sQuery(id+"F0.wireOp",EDGE,"E12.3.24.0"),sQuery(id+"F0.wireOp",EDGE,"E12.6.24.0"),sQuery(id+"F0.wireOp",EDGE,"E12.2.25.0"),sQuery(id+"F0.wireOp",EDGE,"E12.3.25.0"),sQuery(id+"F0.wireOp",EDGE,"E12.6.25.0"),sQuery(id+"F0.wireOp",EDGE,"E12.2.26.0"),sQuery(id+"F0.wireOp",EDGE,"E12.3.26.0"),sQuery(id+"F0.wireOp",EDGE,"E12.6.26.0"),sQuery(id+"F0.wireOp",EDGE,"E12.2.27.0"),sQuery(id+"F0.wireOp",EDGE,"E12.3.27.0"),sQuery(id+"F0.wireOp",EDGE,"E12.6.27.0"),sQuery(id+"F0.wireOp",EDGE,"E12.2.28.0"),sQuery(id+"F0.wireOp",EDGE,"E12.3.28.0"),sQuery(id+"F0.wireOp",EDGE,"E12.6.28.0"),sQuery(id+"F0.wireOp",EDGE,"E12.2.29.0"),sQuery(id+"F0.wireOp",EDGE,"E12.3.29.0"),sQuery(id+"F0.wireOp",EDGE,"E12.6.29.0"),sQuery(id+"F0.wireOp",EDGE,"E12.2.30.0"),sQuery(id+"F0.wireOp",EDGE,"E12.3.30.0"),sQuery(id+"F0.wireOp",EDGE,"E12.6.30.0"),sQuery(id+"F0.wireOp",EDGE,"E12.2.31.0"),sQuery(id+"F0.wireOp",EDGE,"E12.3.31.0"),sQuery(id+"F0.wireOp",EDGE,"E12.6.31.0"),sQuery(id+"F0.wireOp",EDGE,"E12.2.32.0"),sQuery(id+"F0.wireOp",EDGE,"E12.3.32.0"),sQuery(id+"F0.wireOp",EDGE,"E12.6.32.0"),sQuery(id+"F0.wireOp",EDGE,"E12.2.33.0"),sQuery(id+"F0.wireOp",EDGE,"E12.3.33.0"),sQuery(id+"F0.wireOp",EDGE,"E12.6.33.0"),sQuery(id+"F0.wireOp",EDGE,"E12.2.34.0"),sQuery(id+"F0.wireOp",EDGE,"E12.3.34.0"),sQuery(id+"F0.wireOp",EDGE,"E12.6.34.0"),sQuery(id+"F0.wireOp",EDGE,"E12.2.35.0"),sQuery(id+"F0.wireOp",EDGE,"E12.3.35.0"),sQuery(id+"F0.wireOp",EDGE,"E12.6.35.0"),sQuery(id+"F0.wireOp",EDGE,"E12.2.36.0"),sQuery(id+"F0.wireOp",EDGE,"E12.3.36.0"),sQuery(id+"F0.wireOp",EDGE,"E12.6.36.0"),sQuery(id+"F0.wireOp",EDGE,"E12.2.37.0"),sQuery(id+"F0.wireOp",EDGE,"E12.3.37.0"),sQuery(id+"F0.wireOp",EDGE,"E12.6.37.0"),sQuery(id+"F0.wireOp",EDGE,"E12.2.38.0"),sQuery(id+"F0.wireOp",EDGE,"E12.3.38.0"),sQuery(id+"F0.wireOp",EDGE,"E12.6.38.0"),sQuery(id+"F0.wireOp",EDGE,"E12.2.39.0"),sQuery(id+"F0.wireOp",EDGE,"E12.3.39.0"),sQuery(id+"F0.wireOp",EDGE,"E12.6.39.0"),sQuery(id+"F0.wireOp",EDGE,"E12.2.40.0"),sQuery(id+"F0.wireOp",EDGE,"E12.3.40.0"),sQuery(id+"F0.wireOp",EDGE,"E12.6.40.0"),sQuery(id+"F0.wireOp",EDGE,"E12.2.41.0"),sQuery(id+"F0.wireOp",EDGE,"E12.3.41.0"),sQuery(id+"F0.wireOp",EDGE,"E12.6.41.0"),sQuery(id+"F0.wireOp",EDGE,"E12.2.42.0"),sQuery(id+"F0.wireOp",EDGE,"E12.3.42.0"),sQuery(id+"F0.wireOp",EDGE,"E12.6.42.0"),sQuery(id+"F0.wireOp",EDGE,"E12.2.43.0"),sQuery(id+"F0.wireOp",EDGE,"E12.3.43.0"),sQuery(id+"F0.wireOp",EDGE,"E12.6.43.0"),sQuery(id+"F0.wireOp",EDGE,"E12.2.44.0"),sQuery(id+"F0.wireOp",EDGE,"E12.3.44.0"),sQuery(id+"F0.wireOp",EDGE,"E12.6.44.0"),sQuery(id+"F0.wireOp",EDGE,"E12.2.45.0"),sQuery(id+"F0.wireOp",EDGE,"E12.3.45.0"),sQuery(id+"F0.wireOp",EDGE,"E12.6.45.0"),sQuery(id+"F0.wireOp",EDGE,"E12.2.46.0"),sQuery(id+"F0.wireOp",EDGE,"E12.3.46.0"),sQuery(id+"F0.wireOp",EDGE,"E12.6.46.0"),sQuery(id+"F0.wireOp",EDGE,"E12.2.47.0"),sQuery(id+"F0.wireOp",EDGE,"E12.3.47.0"),sQuery(id+"F0.wireOp",EDGE,"E12.6.47.0"),sQuery(id+"F0.wireOp",EDGE,"E12.2.48.0"),sQuery(id+"F0.wireOp",EDGE,"E12.3.48.0"),sQuery(id+"F0.wireOp",EDGE,"E12.6.48.0"),sQuery(id+"F0.wireOp",EDGE,"E12.2.49.0"),sQuery(id+"F0.wireOp",EDGE,"E12.3.49.0"),sQuery(id+"F0.wireOp",EDGE,"E12.6.49.0"),sQuery(id+"F0.wireOp",EDGE,"E12.2.50.0"),sQuery(id+"F0.wireOp",EDGE,"E12.3.50.0"),sQuery(id+"F0.wireOp",EDGE,"E12.6.50.0"),sQuery(id+"F0.wireOp",EDGE,"E12.2.51.0"),sQuery(id+"F0.wireOp",EDGE,"E12.3.51.0"),sQuery(id+"F0.wireOp",EDGE,"E12.6.51.0"),sQuery(id+"F0.wireOp",EDGE,"E12.2.52.0"),sQuery(id+"F0.wireOp",EDGE,"E12.3.52.0"),sQuery(id+"F0.wireOp",EDGE,"E12.6.52.0"),sQuery(id+"F0.wireOp",EDGE,"E12.2.53.0"),sQuery(id+"F0.wireOp",EDGE,"E12.3.53.0"),sQuery(id+"F0.wireOp",EDGE,"E12.6.53.0"),sQuery(id+"F0.wireOp",EDGE,"E12.2.54.0"),sQuery(id+"F0.wireOp",EDGE,"E12.3.54.0"),sQuery(id+"F0.wireOp",EDGE,"E12.6.54.0"),sQuery(id+"F0.wireOp",EDGE,"E12.2.55.0"),sQuery(id+"F0.wireOp",EDGE,"E12.3.55.0"),sQuery(id+"F0.wireOp",EDGE,"E12.6.55.0"),sQuery(id+"F0.wireOp",EDGE,"E12.2.56.0"),sQuery(id+"F0.wireOp",EDGE,"E12.3.56.0"),sQuery(id+"F0.wireOp",EDGE,"E12.6.56.0"),sQuery(id+"F0.wireOp",EDGE,"E12.2.57.0"),sQuery(id+"F0.wireOp",EDGE,"E12.3.57.0"),sQuery(id+"F0.wireOp",EDGE,"E12.6.57.0"),sQuery(id+"F0.wireOp",EDGE,"E12.2.58.0"),sQuery(id+"F0.wireOp",EDGE,"E12.3.58.0"),sQuery(id+"F0.wireOp",EDGE,"E12.6.58.0"),sQuery(id+"F0.wireOp",EDGE,"E12.2.59.0"),sQuery(id+"F0.wireOp",EDGE,"E12.3.59.0"),sQuery(id+"F0.wireOp",EDGE,"E12.6.59.0"),sQuery(id+"F0.wireOp",EDGE,"E13.2.60.0"),sQuery(id+"F0.wireOp",EDGE,"E13.3.60.0"),sQuery(id+"F0.wireOp",EDGE,"E13.6.60.0"),sQuery(id+"F0.wireOp",EDGE,"E13.2.61.0"),sQuery(id+"F0.wireOp",EDGE,"E13.3.61.0"),sQuery(id+"F0.wireOp",EDGE,"E13.6.61.0"),sQuery(id+"F0.wireOp",EDGE,"E13.2.62.0"),sQuery(id+"F0.wireOp",EDGE,"E13.3.62.0"),sQuery(id+"F0.wireOp",EDGE,"E13.6.62.0"),sQuery(id+"F0.wireOp",EDGE,"E13.2.63.0"),sQuery(id+"F0.wireOp",EDGE,"E13.3.63.0"),sQuery(id+"F0.wireOp",EDGE,"E13.6.63.0"),sQuery(id+"F0.wireOp",EDGE,"E13.2.64.0"),sQuery(id+"F0.wireOp",EDGE,"E13.3.64.0"),sQuery(id+"F0.wireOp",EDGE,"E13.6.64.0"),sQuery(id+"F0.wireOp",EDGE,"E13.2.65.0"),sQuery(id+"F0.wireOp",EDGE,"E13.3.65.0"),sQuery(id+"F0.wireOp",EDGE,"E13.6.65.0"),sQuery(id+"F0.wireOp",EDGE,"E13.2.66.0"),sQuery(id+"F0.wireOp",EDGE,"E13.3.66.0"),sQuery(id+"F0.wireOp",EDGE,"E13.6.66.0"),sQuery(id+"F0.wireOp",EDGE,"E13.2.67.0"),sQuery(id+"F0.wireOp",EDGE,"E13.3.67.0"),sQuery(id+"F0.wireOp",EDGE,"E13.6.67.0"),sQuery(id+"F0.wireOp",EDGE,"E13.2.68.0"),sQuery(id+"F0.wireOp",EDGE,"E13.3.68.0"),sQuery(id+"F0.wireOp",EDGE,"E13.6.68.0"),sQuery(id+"F0.wireOp",EDGE,"E13.2.69.0"),sQuery(id+"F0.wireOp",EDGE,"E13.3.69.0"),sQuery(id+"F0.wireOp",EDGE,"E13.6.69.0"),sQuery(id+"F0.wireOp",EDGE,"E13.2.70.0"),sQuery(id+"F0.wireOp",EDGE,"E13.3.70.0"),sQuery(id+"F0.wireOp",EDGE,"E13.6.70.0"),sQuery(id+"F0.wireOp",EDGE,"E13.2.71.0"),sQuery(id+"F0.wireOp",EDGE,"E13.3.71.0"),sQuery(id+"F0.wireOp",EDGE,"E13.6.71.0"),sQuery(id+"F0.wireOp",EDGE,"E13.2.72.0"),sQuery(id+"F0.wireOp",EDGE,"E13.3.72.0"),sQuery(id+"F0.wireOp",EDGE,"E13.6.72.0"),sQuery(id+"F0.wireOp",EDGE,"E13.2.73.0"),sQuery(id+"F0.wireOp",EDGE,"E13.3.73.0"),sQuery(id+"F0.wireOp",EDGE,"E13.6.73.0"),sQuery(id+"F0.wireOp",EDGE,"E13.2.74.0"),sQuery(id+"F0.wireOp",EDGE,"E13.3.74.0"),sQuery(id+"F0.wireOp",EDGE,"E13.6.74.0"),sQuery(id+"F0.wireOp",EDGE,"E13.2.75.0"),sQuery(id+"F0.wireOp",EDGE,"E13.3.75.0"),sQuery(id+"F0.wireOp",EDGE,"E13.6.75.0"),sQuery(id+"F0.wireOp",EDGE,"E13.2.76.0"),sQuery(id+"F0.wireOp",EDGE,"E13.3.76.0"),sQuery(id+"F0.wireOp",EDGE,"E13.6.76.0"),sQuery(id+"F0.wireOp",EDGE,"E13.2.77.0"),sQuery(id+"F0.wireOp",EDGE,"E13.3.77.0"),sQuery(id+"F0.wireOp",EDGE,"E13.6.77.0"),sQuery(id+"F0.wireOp",EDGE,"E13.2.78.0"),sQuery(id+"F0.wireOp",EDGE,"E13.3.78.0"),sQuery(id+"F0.wireOp",EDGE,"E13.6.78.0"),sQuery(id+"F0.wireOp",EDGE,"E13.2.79.0"),sQuery(id+"F0.wireOp",EDGE,"E13.3.79.0"),sQuery(id+"F0.wireOp",EDGE,"E13.6.79.0"),sQuery(id+"F0.wireOp",EDGE,"E13.2.80.0"),sQuery(id+"F0.wireOp",EDGE,"E13.3.80.0"),sQuery(id+"F0.wireOp",EDGE,"E13.6.80.0"),sQuery(id+"F0.wireOp",EDGE,"E13.2.81.0"),sQuery(id+"F0.wireOp",EDGE,"E13.3.81.0"),sQuery(id+"F0.wireOp",EDGE,"E13.6.81.0"),sQuery(id+"F0.wireOp",EDGE,"E13.2.82.0"),sQuery(id+"F0.wireOp",EDGE,"E13.3.82.0"),sQuery(id+"F0.wireOp",EDGE,"E13.6.82.0"),sQuery(id+"F0.wireOp",EDGE,"E13.2.83.0"),sQuery(id+"F0.wireOp",EDGE,"E13.3.83.0"),sQuery(id+"F0.wireOp",EDGE,"E13.6.83.0"),sQuery(id+"F0.wireOp",EDGE,"E13.2.84.0"),sQuery(id+"F0.wireOp",EDGE,"E13.3.84.0"),sQuery(id+"F0.wireOp",EDGE,"E13.6.84.0"),sQuery(id+"F0.wireOp",EDGE,"E13.2.85.0"),sQuery(id+"F0.wireOp",EDGE,"E13.3.85.0"),sQuery(id+"F0.wireOp",EDGE,"E13.6.85.0"),sQuery(id+"F0.wireOp",EDGE,"E13.2.86.0"),sQuery(id+"F0.wireOp",EDGE,"E13.3.86.0"),sQuery(id+"F0.wireOp",EDGE,"E13.6.86.0"),sQuery(id+"F0.wireOp",EDGE,"E13.2.87.0"),sQuery(id+"F0.wireOp",EDGE,"E13.3.87.0"),sQuery(id+"F0.wireOp",EDGE,"E13.6.87.0"),sQuery(id+"F0.wireOp",EDGE,"E13.2.88.0"),sQuery(id+"F0.wireOp",EDGE,"E13.3.88.0"),sQuery(id+"F0.wireOp",EDGE,"E13.6.88.0"),sQuery(id+"F0.wireOp",EDGE,"E13.2.89.0"),sQuery(id+"F0.wireOp",EDGE,"E13.3.89.0"),sQuery(id+"F0.wireOp",EDGE,"E13.6.89.0"),sQuery(id+"F0.wireOp",EDGE,"E13.2.90.0"),sQuery(id+"F0.wireOp",EDGE,"E13.3.90.0"),sQuery(id+"F0.wireOp",EDGE,"E13.6.90.0"),sQuery(id+"F0.wireOp",EDGE,"E13.2.91.0"),sQuery(id+"F0.wireOp",EDGE,"E13.3.91.0"),sQuery(id+"F0.wireOp",EDGE,"E13.6.91.0"),sQuery(id+"F0.wireOp",EDGE,"E13.2.92.0"),sQuery(id+"F0.wireOp",EDGE,"E13.3.92.0"),sQuery(id+"F0.wireOp",EDGE,"E13.6.92.0"),sQuery(id+"F0.wireOp",EDGE,"E13.2.93.0"),sQuery(id+"F0.wireOp",EDGE,"E13.3.93.0"),sQuery(id+"F0.wireOp",EDGE,"E13.6.93.0"),sQuery(id+"F0.wireOp",EDGE,"E13.2.94.0"),sQuery(id+"F0.wireOp",EDGE,"E13.3.94.0"),sQuery(id+"F0.wireOp",EDGE,"E13.6.94.0"),sQuery(id+"F0.wireOp",EDGE,"E13.2.95.0"),sQuery(id+"F0.wireOp",EDGE,"E13.3.95.0"),sQuery(id+"F0.wireOp",EDGE,"E13.6.95.0"),sQuery(id+"F0.wireOp",EDGE,"E13.2.96.0"),sQuery(id+"F0.wireOp",EDGE,"E13.3.96.0"),sQuery(id+"F0.wireOp",EDGE,"E13.6.96.0"),sQuery(id+"F0.wireOp",EDGE,"E13.2.97.0"),sQuery(id+"F0.wireOp",EDGE,"E13.3.97.0"),sQuery(id+"F0.wireOp",EDGE,"E13.6.97.0"),sQuery(id+"F0.wireOp",EDGE,"E13.2.98.0"),sQuery(id+"F0.wireOp",EDGE,"E13.3.98.0"),sQuery(id+"F0.wireOp",EDGE,"E13.6.98.0"),sQuery(id+"F0.wireOp",EDGE,"E13.2.99.0"),sQuery(id+"F0.wireOp",EDGE,"E13.3.99.0"),sQuery(id+"F0.wireOp",EDGE,"E13.6.99.0"),sQuery(id+"F0.wireOp",EDGE,"E13.2.100.0"),sQuery(id+"F0.wireOp",EDGE,"E13.3.100.0"),sQuery(id+"F0.wireOp",EDGE,"E13.6.100.0"),sQuery(id+"F0.wireOp",EDGE,"E13.2.101.0"),sQuery(id+"F0.wireOp",EDGE,"E13.3.101.0"),sQuery(id+"F0.wireOp",EDGE,"E13.6.101.0"),sQuery(id+"F0.wireOp",EDGE,"E13.2.102.0"),sQuery(id+"F0.wireOp",EDGE,"E13.3.102.0"),sQuery(id+"F0.wireOp",EDGE,"E13.6.102.0"),sQuery(id+"F0.wireOp",EDGE,"E13.2.103.0"),sQuery(id+"F0.wireOp",EDGE,"E13.3.103.0"),sQuery(id+"F0.wireOp",EDGE,"E13.6.103.0"),sQuery(id+"F0.wireOp",EDGE,"E13.2.104.0"),sQuery(id+"F0.wireOp",EDGE,"E13.3.104.0"),sQuery(id+"F0.wireOp",EDGE,"E13.6.104.0"),sQuery(id+"F0.wireOp",EDGE,"E13.2.105.0"),sQuery(id+"F0.wireOp",EDGE,"E13.3.105.0"),sQuery(id+"F0.wireOp",EDGE,"E13.6.105.0"),sQuery(id+"F0.wireOp",EDGE,"E13.2.106.0"),sQuery(id+"F0.wireOp",EDGE,"E13.3.106.0"),sQuery(id+"F0.wireOp",EDGE,"E13.6.106.0"),sQuery(id+"F0.wireOp",EDGE,"E13.2.107.0"),sQuery(id+"F0.wireOp",EDGE,"E13.3.107.0"),sQuery(id+"F0.wireOp",EDGE,"E13.6.107.0"),sQuery(id+"F0.wireOp",EDGE,"E13.2.108.0"),sQuery(id+"F0.wireOp",EDGE,"E13.3.108.0"),sQuery(id+"F0.wireOp",EDGE,"E13.6.108.0"),sQuery(id+"F0.wireOp",EDGE,"E13.2.109.0"),sQuery(id+"F0.wireOp",EDGE,"E13.3.109.0"),sQuery(id+"F0.wireOp",EDGE,"E13.6.109.0"),sQuery(id+"F0.wireOp",EDGE,"E13.2.110.0"),sQuery(id+"F0.wireOp",EDGE,"E13.3.110.0"),sQuery(id+"F0.wireOp",EDGE,"E13.6.110.0"),sQuery(id+"F0.wireOp",EDGE,"E13.2.111.0"),sQuery(id+"F0.wireOp",EDGE,"E13.3.111.0"),sQuery(id+"F0.wireOp",EDGE,"E13.6.111.0"),sQuery(id+"F0.wireOp",EDGE,"E13.2.112.0"),sQuery(id+"F0.wireOp",EDGE,"E13.3.112.0"),sQuery(id+"F0.wireOp",EDGE,"E13.6.112.0"),sQuery(id+"F0.wireOp",EDGE,"E13.2.113.0"),sQuery(id+"F0.wireOp",EDGE,"E13.3.113.0"),sQuery(id+"F0.wireOp",EDGE,"E13.6.113.0"),sQuery(id+"F0.wireOp",EDGE,"E13.2.114.0"),sQuery(id+"F0.wireOp",EDGE,"E13.3.114.0"),sQuery(id+"F0.wireOp",EDGE,"E13.6.114.0"),sQuery(id+"F0.wireOp",EDGE,"E13.2.115.0"),sQuery(id+"F0.wireOp",EDGE,"E13.3.115.0"),sQuery(id+"F0.wireOp",EDGE,"E13.6.115.0"),sQuery(id+"F0.wireOp",EDGE,"E13.2.116.0"),sQuery(id+"F0.wireOp",EDGE,"E13.3.116.0"),sQuery(id+"F0.wireOp",EDGE,"E13.6.116.0"),sQuery(id+"F0.wireOp",EDGE,"E13.2.117.0"),sQuery(id+"F0.wireOp",EDGE,"E13.3.117.0"),sQuery(id+"F0.wireOp",EDGE,"E13.6.117.0"),sQuery(id+"F0.wireOp",EDGE,"E13.2.118.0"),sQuery(id+"F0.wireOp",EDGE,"E13.3.118.0"),sQuery(id+"F0.wireOp",EDGE,"E13.6.118.0"),sQuery(id+"F0.wireOp",EDGE,"E13.2.119.0"),sQuery(id+"F0.wireOp",EDGE,"E13.3.119.0"),sQuery(id+"F0.wireOp",EDGE,"E13.6.119.0"),sQuery(id+"F0.wireOp",EDGE,"E14")])],"isStart":false});
            extrude(context, id + "F5", {"entities" : qUnion([Q0, Q1]), "operationType" : NewBodyOperationType.ADD, "depth" : -3 * mm, "offsetDistance" : 25 * mm});
        }
    });
